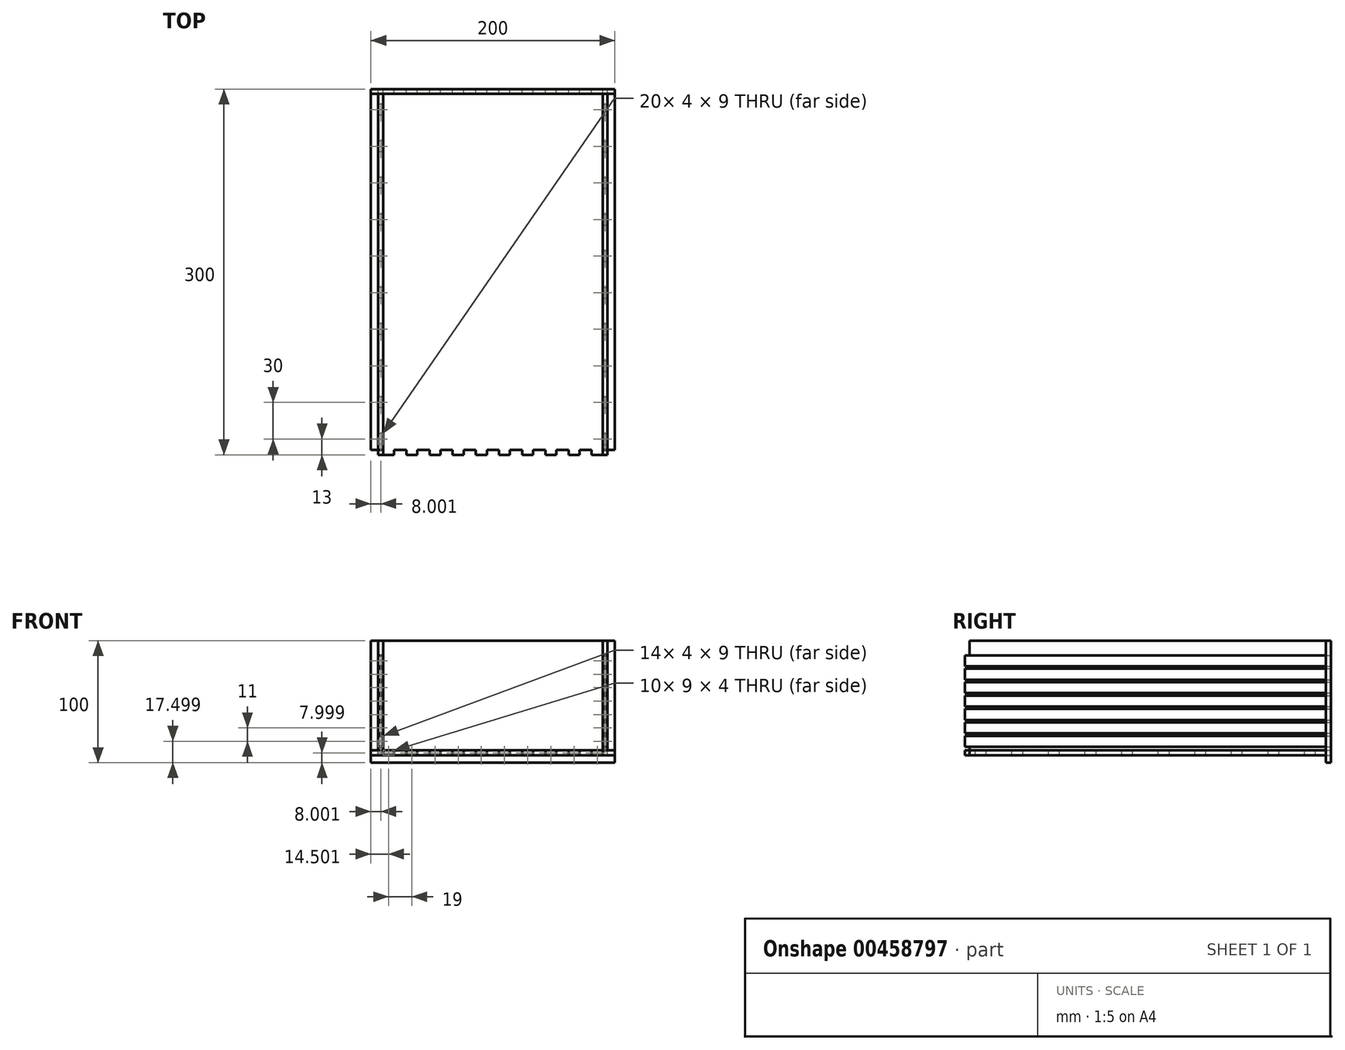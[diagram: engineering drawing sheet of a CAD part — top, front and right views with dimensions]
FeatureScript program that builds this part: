
annotation { "Feature Type Name" : "Feature", "Feature Type Description" : "" }
export const myFeature = defineFeature(function(context is Context, id is Id, definition is map)
    precondition{}
    {
        {
            var Q0;
            Q0=qCreatedBy(makeId("Front.planeOp"),FACE);
            var sketch = newSketch(context, id + "F0", { "sketchPlane" : qUnion([Q0])});
            skLineSegment(sketch, "E0.bottom", {"start": v(-98.88, 5.23) * mm, "end": v(101.12, 5.23) * mm});
            skLineSegment(sketch, "E0.top", {"start": v(-98.88, -94.77) * mm, "end": v(101.12, -94.77) * mm});
            skLineSegment(sketch, "E0.left", {"start": v(-98.88, 5.23) * mm, "end": v(-98.88, -94.77) * mm});
            skLineSegment(sketch, "E0.right", {"start": v(101.12, 5.23) * mm, "end": v(101.12, -94.77) * mm});
            skLineSegment(sketch, "E1.0", {"start": v(-88.88, -4.77) * mm, "end": v(91.12, -4.77) * mm, "construction": true});
            skLineSegment(sketch, "E1.2", {"start": v(-88.88, -84.77) * mm, "end": v(91.12, -84.77) * mm, "construction": true});
            skLineSegment(sketch, "E2.bottom", {"start": v(-88.88, -4.77) * mm, "end": v(-79.88, -4.77) * mm});
            skLineSegment(sketch, "E3.direction1", {"start": v(-88.88, -4.77) * mm, "end": v(-69.88, -4.77) * mm, "construction": true});
            skLineSegment(sketch, "E4.0.9.0", {"start": v(82.12, -4.77) * mm, "end": v(91.12, -4.77) * mm});
            skLineSegment(sketch, "E5", {"start": v(-98.88, -44.77) * mm, "end": v(101.12, -44.77) * mm, "construction": true});
            skLineSegment(sketch, "E6.MirrorCS", {"start": v(-88.88, -84.77) * mm, "end": v(-88.88, -88.77) * mm});
            skLineSegment(sketch, "E7.MirrorCS", {"start": v(-79.88, -84.77) * mm, "end": v(-79.88, -88.77) * mm});
            skLineSegment(sketch, "E8.MirrorCS", {"start": v(-88.88, -88.77) * mm, "end": v(-79.88, -88.77) * mm});
            skLineSegment(sketch, "E9.MirrorCS", {"start": v(-88.88, -84.77) * mm, "end": v(-79.88, -84.77) * mm});
            skLineSegment(sketch, "E10.1.0.0", {"start": v(-60.88, -84.77) * mm, "end": v(-60.88, -88.77) * mm});
            skLineSegment(sketch, "E10.1.0.1", {"start": v(-69.88, -88.77) * mm, "end": v(-60.88, -88.77) * mm});
            skLineSegment(sketch, "E10.1.0.2", {"start": v(-69.88, -84.77) * mm, "end": v(-69.88, -88.77) * mm});
            skLineSegment(sketch, "E10.1.0.3", {"start": v(-69.88, -84.77) * mm, "end": v(-60.88, -84.77) * mm});
            skLineSegment(sketch, "E10.2.0.0", {"start": v(-41.88, -84.77) * mm, "end": v(-41.88, -88.77) * mm});
            skLineSegment(sketch, "E10.2.0.1", {"start": v(-50.88, -88.77) * mm, "end": v(-41.88, -88.77) * mm});
            skLineSegment(sketch, "E10.2.0.2", {"start": v(-50.88, -84.77) * mm, "end": v(-50.88, -88.77) * mm});
            skLineSegment(sketch, "E10.2.0.3", {"start": v(-50.88, -84.77) * mm, "end": v(-41.88, -84.77) * mm});
            skLineSegment(sketch, "E10.3.0.0", {"start": v(-22.88, -84.77) * mm, "end": v(-22.88, -88.77) * mm});
            skLineSegment(sketch, "E10.3.0.1", {"start": v(-31.88, -88.77) * mm, "end": v(-22.88, -88.77) * mm});
            skLineSegment(sketch, "E10.3.0.2", {"start": v(-31.88, -84.77) * mm, "end": v(-31.88, -88.77) * mm});
            skLineSegment(sketch, "E10.3.0.3", {"start": v(-31.88, -84.77) * mm, "end": v(-22.88, -84.77) * mm});
            skLineSegment(sketch, "E10.4.0.0", {"start": v(-3.88, -84.77) * mm, "end": v(-3.88, -88.77) * mm});
            skLineSegment(sketch, "E10.4.0.1", {"start": v(-12.88, -88.77) * mm, "end": v(-3.88, -88.77) * mm});
            skLineSegment(sketch, "E10.4.0.2", {"start": v(-12.88, -84.77) * mm, "end": v(-12.88, -88.77) * mm});
            skLineSegment(sketch, "E10.4.0.3", {"start": v(-12.88, -84.77) * mm, "end": v(-3.88, -84.77) * mm});
            skLineSegment(sketch, "E10.5.0.0", {"start": v(15.12, -84.77) * mm, "end": v(15.12, -88.77) * mm});
            skLineSegment(sketch, "E10.5.0.1", {"start": v(6.12, -88.77) * mm, "end": v(15.12, -88.77) * mm});
            skLineSegment(sketch, "E10.5.0.2", {"start": v(6.12, -84.77) * mm, "end": v(6.12, -88.77) * mm});
            skLineSegment(sketch, "E10.5.0.3", {"start": v(6.12, -84.77) * mm, "end": v(15.12, -84.77) * mm});
            skLineSegment(sketch, "E10.6.0.0", {"start": v(34.12, -84.77) * mm, "end": v(34.12, -88.77) * mm});
            skLineSegment(sketch, "E10.6.0.1", {"start": v(25.12, -88.77) * mm, "end": v(34.12, -88.77) * mm});
            skLineSegment(sketch, "E10.6.0.2", {"start": v(25.12, -84.77) * mm, "end": v(25.12, -88.77) * mm});
            skLineSegment(sketch, "E10.6.0.3", {"start": v(25.12, -84.77) * mm, "end": v(34.12, -84.77) * mm});
            skLineSegment(sketch, "E10.7.0.0", {"start": v(53.12, -84.77) * mm, "end": v(53.12, -88.77) * mm});
            skLineSegment(sketch, "E10.7.0.1", {"start": v(44.12, -88.77) * mm, "end": v(53.12, -88.77) * mm});
            skLineSegment(sketch, "E10.7.0.2", {"start": v(44.12, -84.77) * mm, "end": v(44.12, -88.77) * mm});
            skLineSegment(sketch, "E10.7.0.3", {"start": v(44.12, -84.77) * mm, "end": v(53.12, -84.77) * mm});
            skLineSegment(sketch, "E10.8.0.0", {"start": v(72.12, -84.77) * mm, "end": v(72.12, -88.77) * mm});
            skLineSegment(sketch, "E10.8.0.1", {"start": v(63.12, -88.77) * mm, "end": v(72.12, -88.77) * mm});
            skLineSegment(sketch, "E10.8.0.2", {"start": v(63.12, -84.77) * mm, "end": v(63.12, -88.77) * mm});
            skLineSegment(sketch, "E10.8.0.3", {"start": v(63.12, -84.77) * mm, "end": v(72.12, -84.77) * mm});
            skLineSegment(sketch, "E10.9.0.0", {"start": v(91.12, -84.77) * mm, "end": v(91.12, -88.77) * mm});
            skLineSegment(sketch, "E10.9.0.1", {"start": v(82.12, -88.77) * mm, "end": v(91.12, -88.77) * mm});
            skLineSegment(sketch, "E10.9.0.2", {"start": v(82.12, -84.77) * mm, "end": v(82.12, -88.77) * mm});
            skLineSegment(sketch, "E10.9.0.3", {"start": v(82.12, -84.77) * mm, "end": v(91.12, -84.77) * mm});
            skLineSegment(sketch, "E10.direction1", {"start": v(-79.88, -88.77) * mm, "end": v(-60.88, -88.77) * mm, "construction": true});
            skLineSegment(sketch, "E11.bottom", {"start": v(-88.88, -81.77) * mm, "end": v(-92.88, -81.77) * mm});
            skLineSegment(sketch, "E11.top", {"start": v(-88.88, -72.77) * mm, "end": v(-92.88, -72.77) * mm});
            skLineSegment(sketch, "E11.left", {"start": v(-88.88, -81.77) * mm, "end": v(-88.88, -72.77) * mm});
            skLineSegment(sketch, "E11.right", {"start": v(-92.88, -81.77) * mm, "end": v(-92.88, -72.77) * mm});
            skLineSegment(sketch, "E12.0.1.0", {"start": v(-88.88, -61.77) * mm, "end": v(-92.88, -61.77) * mm});
            skLineSegment(sketch, "E12.0.1.1", {"start": v(-92.88, -70.77) * mm, "end": v(-92.88, -61.77) * mm});
            skLineSegment(sketch, "E12.0.1.2", {"start": v(-88.88, -70.77) * mm, "end": v(-92.88, -70.77) * mm});
            skLineSegment(sketch, "E12.0.1.3", {"start": v(-88.88, -70.77) * mm, "end": v(-88.88, -61.77) * mm});
            skLineSegment(sketch, "E12.0.2.0", {"start": v(-88.88, -50.77) * mm, "end": v(-92.88, -50.77) * mm});
            skLineSegment(sketch, "E12.0.2.1", {"start": v(-92.88, -59.77) * mm, "end": v(-92.88, -50.77) * mm});
            skLineSegment(sketch, "E12.0.2.2", {"start": v(-88.88, -59.77) * mm, "end": v(-92.88, -59.77) * mm});
            skLineSegment(sketch, "E12.0.2.3", {"start": v(-88.88, -59.77) * mm, "end": v(-88.88, -50.77) * mm});
            skLineSegment(sketch, "E12.0.3.0", {"start": v(-88.88, -39.77) * mm, "end": v(-92.88, -39.77) * mm});
            skLineSegment(sketch, "E12.0.3.1", {"start": v(-92.88, -48.77) * mm, "end": v(-92.88, -39.77) * mm});
            skLineSegment(sketch, "E12.0.3.2", {"start": v(-88.88, -48.77) * mm, "end": v(-92.88, -48.77) * mm});
            skLineSegment(sketch, "E12.0.3.3", {"start": v(-88.88, -48.77) * mm, "end": v(-88.88, -39.77) * mm});
            skLineSegment(sketch, "E12.0.4.0", {"start": v(-88.88, -28.77) * mm, "end": v(-92.88, -28.77) * mm});
            skLineSegment(sketch, "E12.0.4.1", {"start": v(-92.88, -37.77) * mm, "end": v(-92.88, -28.77) * mm});
            skLineSegment(sketch, "E12.0.4.2", {"start": v(-88.88, -37.77) * mm, "end": v(-92.88, -37.77) * mm});
            skLineSegment(sketch, "E12.0.4.3", {"start": v(-88.88, -37.77) * mm, "end": v(-88.88, -28.77) * mm});
            skLineSegment(sketch, "E12.0.5.0", {"start": v(-88.88, -17.77) * mm, "end": v(-92.88, -17.77) * mm});
            skLineSegment(sketch, "E12.0.5.1", {"start": v(-92.88, -26.77) * mm, "end": v(-92.88, -17.77) * mm});
            skLineSegment(sketch, "E12.0.5.2", {"start": v(-88.88, -26.77) * mm, "end": v(-92.88, -26.77) * mm});
            skLineSegment(sketch, "E12.0.5.3", {"start": v(-88.88, -26.77) * mm, "end": v(-88.88, -17.77) * mm});
            skLineSegment(sketch, "E12.0.6.0", {"start": v(-88.88, -6.77) * mm, "end": v(-92.88, -6.77) * mm});
            skLineSegment(sketch, "E12.0.6.1", {"start": v(-92.88, -15.77) * mm, "end": v(-92.88, -6.77) * mm});
            skLineSegment(sketch, "E12.0.6.2", {"start": v(-88.88, -15.77) * mm, "end": v(-92.88, -15.77) * mm});
            skLineSegment(sketch, "E12.0.6.3", {"start": v(-88.88, -15.77) * mm, "end": v(-88.88, -6.77) * mm});
            skLineSegment(sketch, "E12.direction1", {"start": v(-92.88, -72.77) * mm, "end": v(-67.88, -72.77) * mm, "construction": true});
            skLineSegment(sketch, "E12.direction2", {"start": v(-92.88, -72.77) * mm, "end": v(-92.88, -61.77) * mm, "construction": true});
            skLineSegment(sketch, "E13", {"start": v(1.12, 5.23) * mm, "end": v(1.12, -94.77) * mm, "construction": true});
            skLineSegment(sketch, "E14.MirrorCS", {"start": v(95.12, -81.77) * mm, "end": v(95.12, -72.77) * mm});
            skLineSegment(sketch, "E15.MirrorCS", {"start": v(91.12, -81.77) * mm, "end": v(95.12, -81.77) * mm});
            skLineSegment(sketch, "E16.MirrorCS", {"start": v(91.12, -81.77) * mm, "end": v(91.12, -72.77) * mm});
            skLineSegment(sketch, "E17.MirrorCS", {"start": v(95.12, -72.77) * mm, "end": v(70.12, -72.77) * mm, "construction": true});
            skLineSegment(sketch, "E18.MirrorCS", {"start": v(91.12, -72.77) * mm, "end": v(95.12, -72.77) * mm});
            skLineSegment(sketch, "E19.0.1.0", {"start": v(91.12, -70.77) * mm, "end": v(91.12, -61.77) * mm});
            skLineSegment(sketch, "E19.0.1.1", {"start": v(91.12, -61.77) * mm, "end": v(95.12, -61.77) * mm});
            skLineSegment(sketch, "E19.0.1.2", {"start": v(95.12, -70.77) * mm, "end": v(95.12, -61.77) * mm});
            skLineSegment(sketch, "E19.0.1.3", {"start": v(91.12, -70.77) * mm, "end": v(95.12, -70.77) * mm});
            skLineSegment(sketch, "E19.0.2.0", {"start": v(91.12, -59.77) * mm, "end": v(91.12, -50.77) * mm});
            skLineSegment(sketch, "E19.0.2.1", {"start": v(91.12, -50.77) * mm, "end": v(95.12, -50.77) * mm});
            skLineSegment(sketch, "E19.0.2.2", {"start": v(95.12, -59.77) * mm, "end": v(95.12, -50.77) * mm});
            skLineSegment(sketch, "E19.0.2.3", {"start": v(91.12, -59.77) * mm, "end": v(95.12, -59.77) * mm});
            skLineSegment(sketch, "E19.0.3.0", {"start": v(91.12, -48.77) * mm, "end": v(91.12, -39.77) * mm});
            skLineSegment(sketch, "E19.0.3.1", {"start": v(91.12, -39.77) * mm, "end": v(95.12, -39.77) * mm});
            skLineSegment(sketch, "E19.0.3.2", {"start": v(95.12, -48.77) * mm, "end": v(95.12, -39.77) * mm});
            skLineSegment(sketch, "E19.0.3.3", {"start": v(91.12, -48.77) * mm, "end": v(95.12, -48.77) * mm});
            skLineSegment(sketch, "E19.0.4.0", {"start": v(91.12, -37.77) * mm, "end": v(91.12, -28.77) * mm});
            skLineSegment(sketch, "E19.0.4.1", {"start": v(91.12, -28.77) * mm, "end": v(95.12, -28.77) * mm});
            skLineSegment(sketch, "E19.0.4.2", {"start": v(95.12, -37.77) * mm, "end": v(95.12, -28.77) * mm});
            skLineSegment(sketch, "E19.0.4.3", {"start": v(91.12, -37.77) * mm, "end": v(95.12, -37.77) * mm});
            skLineSegment(sketch, "E19.0.5.0", {"start": v(91.12, -26.77) * mm, "end": v(91.12, -17.77) * mm});
            skLineSegment(sketch, "E19.0.5.1", {"start": v(91.12, -17.77) * mm, "end": v(95.12, -17.77) * mm});
            skLineSegment(sketch, "E19.0.5.2", {"start": v(95.12, -26.77) * mm, "end": v(95.12, -17.77) * mm});
            skLineSegment(sketch, "E19.0.5.3", {"start": v(91.12, -26.77) * mm, "end": v(95.12, -26.77) * mm});
            skLineSegment(sketch, "E19.0.6.0", {"start": v(91.12, -15.77) * mm, "end": v(91.12, -6.77) * mm});
            skLineSegment(sketch, "E19.0.6.1", {"start": v(91.12, -6.77) * mm, "end": v(95.12, -6.77) * mm});
            skLineSegment(sketch, "E19.0.6.2", {"start": v(95.12, -15.77) * mm, "end": v(95.12, -6.77) * mm});
            skLineSegment(sketch, "E19.0.6.3", {"start": v(91.12, -15.77) * mm, "end": v(95.12, -15.77) * mm});
            skLineSegment(sketch, "E19.direction1", {"start": v(91.12, -81.77) * mm, "end": v(116.12, -81.77) * mm, "construction": true});
            skLineSegment(sketch, "E19.direction2", {"start": v(91.12, -81.77) * mm, "end": v(91.12, -70.77) * mm, "construction": true});
            skLineSegment(sketch, "E20", {"start": v(-84.38, -84.77) * mm, "end": v(-84.38, 5.23) * mm, "construction": true});
            skLineSegment(sketch, "E21.MirrorCS", {"start": v(86.62, -84.77) * mm, "end": v(86.62, 5.23) * mm, "construction": true});
            skSolve(sketch);
        }
        {
            var Q0;
            Q0=makeQuery(id+"F0.imprint","IMPRINT",FACE,{"disambiguationData":[TD([[makeQuery(id+"F0.imprint","IMPRINT",EDGE,{"derivedFrom":sQuery(id+"F0.wireOp",EDGE,"E0.bottom")}),-1.0]])]});
            extrude(context, id + "F1", {"entities" : qUnion([Q0]), "depth" : 4 * mm});
        }
        {
            var Q0;
            Q0=makeQuery(id+"F0.imprint","IMPRINT",FACE,{"disambiguationData":[TD([[makeQuery(id+"F0.imprint","IMPRINT",EDGE,{"derivedFrom":sQuery(id+"F0.wireOp",EDGE,"E10.8.0.0")}),-1.0]])]});
            var Q1;
            Q1=makeQuery(id+"F0.imprint","IMPRINT",FACE,{"disambiguationData":[TD([[makeQuery(id+"F0.imprint","IMPRINT",EDGE,{"derivedFrom":sQuery(id+"F0.wireOp",EDGE,"E10.7.0.0")}),-1.0]])]});
            var Q2;
            Q2=makeQuery(id+"F0.imprint","IMPRINT",FACE,{"disambiguationData":[TD([[makeQuery(id+"F0.imprint","IMPRINT",EDGE,{"derivedFrom":sQuery(id+"F0.wireOp",EDGE,"E10.9.0.0")}),-1.0]])]});
            var Q3;
            Q3=makeQuery(id+"F0.imprint","IMPRINT",FACE,{"disambiguationData":[TD([[makeQuery(id+"F0.imprint","IMPRINT",EDGE,{"derivedFrom":sQuery(id+"F0.wireOp",EDGE,"E10.6.0.0")}),-1.0]])]});
            var Q4;
            Q4=makeQuery(id+"F0.imprint","IMPRINT",FACE,{"disambiguationData":[TD([[makeQuery(id+"F0.imprint","IMPRINT",EDGE,{"derivedFrom":sQuery(id+"F0.wireOp",EDGE,"E10.5.0.0")}),-1.0]])]});
            var Q5;
            Q5=makeQuery(id+"F0.imprint","IMPRINT",FACE,{"disambiguationData":[TD([[makeQuery(id+"F0.imprint","IMPRINT",EDGE,{"derivedFrom":sQuery(id+"F0.wireOp",EDGE,"E10.4.0.0")}),-1.0]])]});
            var Q6;
            Q6=makeQuery(id+"F0.imprint","IMPRINT",FACE,{"disambiguationData":[TD([[makeQuery(id+"F0.imprint","IMPRINT",EDGE,{"derivedFrom":sQuery(id+"F0.wireOp",EDGE,"E10.3.0.0")}),-1.0]])]});
            var Q7;
            Q7=makeQuery(id+"F0.imprint","IMPRINT",FACE,{"disambiguationData":[TD([[makeQuery(id+"F0.imprint","IMPRINT",EDGE,{"derivedFrom":sQuery(id+"F0.wireOp",EDGE,"E10.2.0.0")}),-1.0]])]});
            var Q8;
            Q8=makeQuery(id+"F0.imprint","IMPRINT",FACE,{"disambiguationData":[TD([[makeQuery(id+"F0.imprint","IMPRINT",EDGE,{"derivedFrom":sQuery(id+"F0.wireOp",EDGE,"E10.1.0.0")}),-1.0]])]});
            var Q9;
            Q9=makeQuery(id+"F0.imprint","IMPRINT",FACE,{"disambiguationData":[TD([[makeQuery(id+"F0.imprint","IMPRINT",EDGE,{"derivedFrom":sQuery(id+"F0.wireOp",EDGE,"E6.MirrorCS")}),1.0]])]});
            extrude(context, id + "F2", {"entities" : qUnion([Q0, Q1, Q2, Q3, Q4, Q5, Q6, Q7, Q8, Q9]), "depth" : 300 * mm});
        }
        {
            var Q0;
            Q0=makeQuery(id+"F1.opExtrude","CAP_FACE",FACE,{"disambiguationData":[OSD([sQuery(id+"F0.wireOp",EDGE,"E0.bottom"),sQuery(id+"F0.wireOp",EDGE,"E0.top"),sQuery(id+"F0.wireOp",EDGE,"E0.left"),sQuery(id+"F0.wireOp",EDGE,"E0.right"),sQuery(id+"F0.wireOp",EDGE,"E6.MirrorCS"),sQuery(id+"F0.wireOp",EDGE,"E7.MirrorCS"),sQuery(id+"F0.wireOp",EDGE,"E8.MirrorCS"),sQuery(id+"F0.wireOp",EDGE,"E9.MirrorCS"),sQuery(id+"F0.wireOp",EDGE,"E10.1.0.0"),sQuery(id+"F0.wireOp",EDGE,"E10.1.0.1"),sQuery(id+"F0.wireOp",EDGE,"E10.1.0.2"),sQuery(id+"F0.wireOp",EDGE,"E10.1.0.3"),sQuery(id+"F0.wireOp",EDGE,"E10.2.0.0"),sQuery(id+"F0.wireOp",EDGE,"E10.2.0.1"),sQuery(id+"F0.wireOp",EDGE,"E10.2.0.2"),sQuery(id+"F0.wireOp",EDGE,"E10.2.0.3"),sQuery(id+"F0.wireOp",EDGE,"E10.3.0.0"),sQuery(id+"F0.wireOp",EDGE,"E10.3.0.1"),sQuery(id+"F0.wireOp",EDGE,"E10.3.0.2"),sQuery(id+"F0.wireOp",EDGE,"E10.3.0.3"),sQuery(id+"F0.wireOp",EDGE,"E10.4.0.0"),sQuery(id+"F0.wireOp",EDGE,"E10.4.0.1"),sQuery(id+"F0.wireOp",EDGE,"E10.4.0.2"),sQuery(id+"F0.wireOp",EDGE,"E10.4.0.3"),sQuery(id+"F0.wireOp",EDGE,"E10.5.0.0"),sQuery(id+"F0.wireOp",EDGE,"E10.5.0.1"),sQuery(id+"F0.wireOp",EDGE,"E10.5.0.2"),sQuery(id+"F0.wireOp",EDGE,"E10.5.0.3"),sQuery(id+"F0.wireOp",EDGE,"E10.6.0.0"),sQuery(id+"F0.wireOp",EDGE,"E10.6.0.1"),sQuery(id+"F0.wireOp",EDGE,"E10.6.0.2"),sQuery(id+"F0.wireOp",EDGE,"E10.6.0.3"),sQuery(id+"F0.wireOp",EDGE,"E10.7.0.0"),sQuery(id+"F0.wireOp",EDGE,"E10.7.0.1"),sQuery(id+"F0.wireOp",EDGE,"E10.7.0.2"),sQuery(id+"F0.wireOp",EDGE,"E10.7.0.3"),sQuery(id+"F0.wireOp",EDGE,"E10.8.0.0"),sQuery(id+"F0.wireOp",EDGE,"E10.8.0.1"),sQuery(id+"F0.wireOp",EDGE,"E10.8.0.2"),sQuery(id+"F0.wireOp",EDGE,"E10.8.0.3"),sQuery(id+"F0.wireOp",EDGE,"E10.9.0.0"),sQuery(id+"F0.wireOp",EDGE,"E10.9.0.1"),sQuery(id+"F0.wireOp",EDGE,"E10.9.0.2"),sQuery(id+"F0.wireOp",EDGE,"E10.9.0.3"),sQuery(id+"F0.wireOp",EDGE,"E11.bottom"),sQuery(id+"F0.wireOp",EDGE,"E11.top"),sQuery(id+"F0.wireOp",EDGE,"E11.left"),sQuery(id+"F0.wireOp",EDGE,"E11.right"),sQuery(id+"F0.wireOp",EDGE,"E12.0.1.0"),sQuery(id+"F0.wireOp",EDGE,"E12.0.1.1"),sQuery(id+"F0.wireOp",EDGE,"E12.0.1.2"),sQuery(id+"F0.wireOp",EDGE,"E12.0.1.3"),sQuery(id+"F0.wireOp",EDGE,"E12.0.2.0"),sQuery(id+"F0.wireOp",EDGE,"E12.0.2.1"),sQuery(id+"F0.wireOp",EDGE,"E12.0.2.2"),sQuery(id+"F0.wireOp",EDGE,"E12.0.2.3"),sQuery(id+"F0.wireOp",EDGE,"E12.0.3.0"),sQuery(id+"F0.wireOp",EDGE,"E12.0.3.1"),sQuery(id+"F0.wireOp",EDGE,"E12.0.3.2"),sQuery(id+"F0.wireOp",EDGE,"E12.0.3.3"),sQuery(id+"F0.wireOp",EDGE,"E12.0.4.0"),sQuery(id+"F0.wireOp",EDGE,"E12.0.4.1"),sQuery(id+"F0.wireOp",EDGE,"E12.0.4.2"),sQuery(id+"F0.wireOp",EDGE,"E12.0.4.3"),sQuery(id+"F0.wireOp",EDGE,"E12.0.5.0"),sQuery(id+"F0.wireOp",EDGE,"E12.0.5.1"),sQuery(id+"F0.wireOp",EDGE,"E12.0.5.2"),sQuery(id+"F0.wireOp",EDGE,"E12.0.5.3"),sQuery(id+"F0.wireOp",EDGE,"E12.0.6.0"),sQuery(id+"F0.wireOp",EDGE,"E12.0.6.1"),sQuery(id+"F0.wireOp",EDGE,"E12.0.6.2"),sQuery(id+"F0.wireOp",EDGE,"E12.0.6.3"),sQuery(id+"F0.wireOp",EDGE,"E14.MirrorCS"),sQuery(id+"F0.wireOp",EDGE,"E15.MirrorCS"),sQuery(id+"F0.wireOp",EDGE,"E16.MirrorCS"),sQuery(id+"F0.wireOp",EDGE,"E18.MirrorCS"),sQuery(id+"F0.wireOp",EDGE,"E19.0.1.0"),sQuery(id+"F0.wireOp",EDGE,"E19.0.1.1"),sQuery(id+"F0.wireOp",EDGE,"E19.0.1.2"),sQuery(id+"F0.wireOp",EDGE,"E19.0.1.3"),sQuery(id+"F0.wireOp",EDGE,"E19.0.2.0"),sQuery(id+"F0.wireOp",EDGE,"E19.0.2.1"),sQuery(id+"F0.wireOp",EDGE,"E19.0.2.2"),sQuery(id+"F0.wireOp",EDGE,"E19.0.2.3"),sQuery(id+"F0.wireOp",EDGE,"E19.0.3.0"),sQuery(id+"F0.wireOp",EDGE,"E19.0.3.1"),sQuery(id+"F0.wireOp",EDGE,"E19.0.3.2"),sQuery(id+"F0.wireOp",EDGE,"E19.0.3.3"),sQuery(id+"F0.wireOp",EDGE,"E19.0.4.0"),sQuery(id+"F0.wireOp",EDGE,"E19.0.4.1"),sQuery(id+"F0.wireOp",EDGE,"E19.0.4.2"),sQuery(id+"F0.wireOp",EDGE,"E19.0.4.3"),sQuery(id+"F0.wireOp",EDGE,"E19.0.5.0"),sQuery(id+"F0.wireOp",EDGE,"E19.0.5.1"),sQuery(id+"F0.wireOp",EDGE,"E19.0.5.2"),sQuery(id+"F0.wireOp",EDGE,"E19.0.5.3"),sQuery(id+"F0.wireOp",EDGE,"E19.0.6.0"),sQuery(id+"F0.wireOp",EDGE,"E19.0.6.1"),sQuery(id+"F0.wireOp",EDGE,"E19.0.6.2"),sQuery(id+"F0.wireOp",EDGE,"E19.0.6.3")])],"isStart":false});
            var sketch = newSketch(context, id + "F3", { "sketchPlane" : qUnion([Q0])});
            skLineSegment(sketch, "E22.bottom", {"start": v(-79.88, -84.77) * mm, "end": v(-69.88, -84.77) * mm});
            skLineSegment(sketch, "E22.top", {"start": v(-79.88, -88.77) * mm, "end": v(-69.88, -88.77) * mm});
            skLineSegment(sketch, "E22.left", {"start": v(-79.88, -84.77) * mm, "end": v(-79.88, -88.77) * mm});
            skLineSegment(sketch, "E22.right", {"start": v(-69.88, -84.77) * mm, "end": v(-69.88, -88.77) * mm});
            skLineSegment(sketch, "E23.1.0.0", {"start": v(-60.88, -84.77) * mm, "end": v(-50.88, -84.77) * mm});
            skLineSegment(sketch, "E23.1.0.1", {"start": v(-60.88, -84.77) * mm, "end": v(-60.88, -88.77) * mm});
            skLineSegment(sketch, "E23.1.0.2", {"start": v(-60.88, -88.77) * mm, "end": v(-50.88, -88.77) * mm});
            skLineSegment(sketch, "E23.1.0.3", {"start": v(-50.88, -84.77) * mm, "end": v(-50.88, -88.77) * mm});
            skLineSegment(sketch, "E23.2.0.0", {"start": v(-41.88, -84.77) * mm, "end": v(-31.88, -84.77) * mm});
            skLineSegment(sketch, "E23.2.0.1", {"start": v(-41.88, -84.77) * mm, "end": v(-41.88, -88.77) * mm});
            skLineSegment(sketch, "E23.2.0.2", {"start": v(-41.88, -88.77) * mm, "end": v(-31.88, -88.77) * mm});
            skLineSegment(sketch, "E23.2.0.3", {"start": v(-31.88, -84.77) * mm, "end": v(-31.88, -88.77) * mm});
            skLineSegment(sketch, "E23.3.0.0", {"start": v(-22.88, -84.77) * mm, "end": v(-12.88, -84.77) * mm});
            skLineSegment(sketch, "E23.3.0.1", {"start": v(-22.88, -84.77) * mm, "end": v(-22.88, -88.77) * mm});
            skLineSegment(sketch, "E23.3.0.2", {"start": v(-22.88, -88.77) * mm, "end": v(-12.88, -88.77) * mm});
            skLineSegment(sketch, "E23.3.0.3", {"start": v(-12.88, -84.77) * mm, "end": v(-12.88, -88.77) * mm});
            skLineSegment(sketch, "E23.4.0.0", {"start": v(-3.88, -84.77) * mm, "end": v(6.12, -84.77) * mm});
            skLineSegment(sketch, "E23.4.0.1", {"start": v(-3.88, -84.77) * mm, "end": v(-3.88, -88.77) * mm});
            skLineSegment(sketch, "E23.4.0.2", {"start": v(-3.88, -88.77) * mm, "end": v(6.12, -88.77) * mm});
            skLineSegment(sketch, "E23.4.0.3", {"start": v(6.12, -84.77) * mm, "end": v(6.12, -88.77) * mm});
            skLineSegment(sketch, "E23.5.0.0", {"start": v(15.12, -84.77) * mm, "end": v(25.12, -84.77) * mm});
            skLineSegment(sketch, "E23.5.0.1", {"start": v(15.12, -84.77) * mm, "end": v(15.12, -88.77) * mm});
            skLineSegment(sketch, "E23.5.0.2", {"start": v(15.12, -88.77) * mm, "end": v(25.12, -88.77) * mm});
            skLineSegment(sketch, "E23.5.0.3", {"start": v(25.12, -84.77) * mm, "end": v(25.12, -88.77) * mm});
            skLineSegment(sketch, "E23.6.0.0", {"start": v(34.12, -84.77) * mm, "end": v(44.12, -84.77) * mm});
            skLineSegment(sketch, "E23.6.0.1", {"start": v(34.12, -84.77) * mm, "end": v(34.12, -88.77) * mm});
            skLineSegment(sketch, "E23.6.0.2", {"start": v(34.12, -88.77) * mm, "end": v(44.12, -88.77) * mm});
            skLineSegment(sketch, "E23.6.0.3", {"start": v(44.12, -84.77) * mm, "end": v(44.12, -88.77) * mm});
            skLineSegment(sketch, "E23.7.0.0", {"start": v(53.12, -84.77) * mm, "end": v(63.12, -84.77) * mm});
            skLineSegment(sketch, "E23.7.0.1", {"start": v(53.12, -84.77) * mm, "end": v(53.12, -88.77) * mm});
            skLineSegment(sketch, "E23.7.0.2", {"start": v(53.12, -88.77) * mm, "end": v(63.12, -88.77) * mm});
            skLineSegment(sketch, "E23.7.0.3", {"start": v(63.12, -84.77) * mm, "end": v(63.12, -88.77) * mm});
            skLineSegment(sketch, "E23.8.0.0", {"start": v(72.12, -84.77) * mm, "end": v(82.12, -84.77) * mm});
            skLineSegment(sketch, "E23.8.0.1", {"start": v(72.12, -84.77) * mm, "end": v(72.12, -88.77) * mm});
            skLineSegment(sketch, "E23.8.0.2", {"start": v(72.12, -88.77) * mm, "end": v(82.12, -88.77) * mm});
            skLineSegment(sketch, "E23.8.0.3", {"start": v(82.12, -84.77) * mm, "end": v(82.12, -88.77) * mm});
            skLineSegment(sketch, "E23.direction1", {"start": v(-79.88, -84.77) * mm, "end": v(-60.88, -84.77) * mm, "construction": true});
            skSolve(sketch);
        }
        {
            var Q0;
            Q0=makeQuery(id+"F3.imprint","IMPRINT",FACE,{"disambiguationData":[TD([[makeQuery(id+"F3.imprint","IMPRINT",EDGE,{"derivedFrom":sQuery(id+"F3.wireOp",EDGE,"E22.bottom")}),-1.0]])]});
            var Q1;
            Q1=makeQuery(id+"F3.imprint","IMPRINT",FACE,{"disambiguationData":[TD([[makeQuery(id+"F3.imprint","IMPRINT",EDGE,{"derivedFrom":sQuery(id+"F3.wireOp",EDGE,"E23.1.0.0")}),-1.0]])]});
            var Q2;
            Q2=makeQuery(id+"F3.imprint","IMPRINT",FACE,{"disambiguationData":[TD([[makeQuery(id+"F3.imprint","IMPRINT",EDGE,{"derivedFrom":sQuery(id+"F3.wireOp",EDGE,"E23.2.0.0")}),-1.0]])]});
            var Q3;
            Q3=makeQuery(id+"F3.imprint","IMPRINT",FACE,{"disambiguationData":[TD([[makeQuery(id+"F3.imprint","IMPRINT",EDGE,{"derivedFrom":sQuery(id+"F3.wireOp",EDGE,"E23.3.0.0")}),-1.0]])]});
            var Q4;
            Q4=makeQuery(id+"F3.imprint","IMPRINT",FACE,{"disambiguationData":[TD([[makeQuery(id+"F3.imprint","IMPRINT",EDGE,{"derivedFrom":sQuery(id+"F3.wireOp",EDGE,"E23.4.0.0")}),-1.0]])]});
            var Q5;
            Q5=makeQuery(id+"F3.imprint","IMPRINT",FACE,{"disambiguationData":[TD([[makeQuery(id+"F3.imprint","IMPRINT",EDGE,{"derivedFrom":sQuery(id+"F3.wireOp",EDGE,"E23.6.0.0")}),-1.0]])]});
            var Q6;
            Q6=makeQuery(id+"F3.imprint","IMPRINT",FACE,{"disambiguationData":[TD([[makeQuery(id+"F3.imprint","IMPRINT",EDGE,{"derivedFrom":sQuery(id+"F3.wireOp",EDGE,"E23.7.0.0")}),-1.0]])]});
            var Q7;
            Q7=makeQuery(id+"F3.imprint","IMPRINT",FACE,{"disambiguationData":[TD([[makeQuery(id+"F3.imprint","IMPRINT",EDGE,{"derivedFrom":sQuery(id+"F3.wireOp",EDGE,"E23.8.0.0")}),-1.0]])]});
            var Q8;
            Q8=makeQuery(id+"F3.imprint","IMPRINT",FACE,{"disambiguationData":[TD([[makeQuery(id+"F3.imprint","IMPRINT",EDGE,{"derivedFrom":sQuery(id+"F3.wireOp",EDGE,"E23.5.0.0")}),-1.0]])]});
            extrude(context, id + "F4", {"entities" : qUnion([Q0, Q1, Q2, Q3, Q4, Q5, Q6, Q7, Q8]), "depth" : 292 * mm});
        }
        {
            var Q0;
            Q0=makeQuery(id+"F2.opExtrude","SWEPT_BODY",BODY,{"disambiguationData":[OSD([sQuery(id+"F0.wireOp",EDGE,"E6.MirrorCS"),sQuery(id+"F0.wireOp",EDGE,"E7.MirrorCS"),sQuery(id+"F0.wireOp",EDGE,"E8.MirrorCS"),sQuery(id+"F0.wireOp",EDGE,"E9.MirrorCS")])]});
            var Q1;
            Q1=makeQuery(id+"F2.opExtrude","SWEPT_BODY",BODY,{"disambiguationData":[OSD([sQuery(id+"F0.wireOp",EDGE,"E10.1.0.0"),sQuery(id+"F0.wireOp",EDGE,"E10.1.0.1"),sQuery(id+"F0.wireOp",EDGE,"E10.1.0.2"),sQuery(id+"F0.wireOp",EDGE,"E10.1.0.3")])]});
            var Q2;
            Q2=makeQuery(id+"F2.opExtrude","SWEPT_BODY",BODY,{"disambiguationData":[OSD([sQuery(id+"F0.wireOp",EDGE,"E10.2.0.0"),sQuery(id+"F0.wireOp",EDGE,"E10.2.0.1"),sQuery(id+"F0.wireOp",EDGE,"E10.2.0.2"),sQuery(id+"F0.wireOp",EDGE,"E10.2.0.3")])]});
            var Q3;
            Q3=makeQuery(id+"F2.opExtrude","SWEPT_BODY",BODY,{"disambiguationData":[OSD([sQuery(id+"F0.wireOp",EDGE,"E10.3.0.0"),sQuery(id+"F0.wireOp",EDGE,"E10.3.0.1"),sQuery(id+"F0.wireOp",EDGE,"E10.3.0.2"),sQuery(id+"F0.wireOp",EDGE,"E10.3.0.3")])]});
            var Q4;
            Q4=makeQuery(id+"F2.opExtrude","SWEPT_BODY",BODY,{"disambiguationData":[OSD([sQuery(id+"F0.wireOp",EDGE,"E10.4.0.0"),sQuery(id+"F0.wireOp",EDGE,"E10.4.0.1"),sQuery(id+"F0.wireOp",EDGE,"E10.4.0.2"),sQuery(id+"F0.wireOp",EDGE,"E10.4.0.3")])]});
            var Q5;
            Q5=makeQuery(id+"F2.opExtrude","SWEPT_BODY",BODY,{"disambiguationData":[OSD([sQuery(id+"F0.wireOp",EDGE,"E10.5.0.0"),sQuery(id+"F0.wireOp",EDGE,"E10.5.0.1"),sQuery(id+"F0.wireOp",EDGE,"E10.5.0.2"),sQuery(id+"F0.wireOp",EDGE,"E10.5.0.3")])]});
            var Q6;
            Q6=makeQuery(id+"F2.opExtrude","SWEPT_BODY",BODY,{"disambiguationData":[OSD([sQuery(id+"F0.wireOp",EDGE,"E10.6.0.0"),sQuery(id+"F0.wireOp",EDGE,"E10.6.0.1"),sQuery(id+"F0.wireOp",EDGE,"E10.6.0.2"),sQuery(id+"F0.wireOp",EDGE,"E10.6.0.3")])]});
            var Q7;
            Q7=makeQuery(id+"F2.opExtrude","SWEPT_BODY",BODY,{"disambiguationData":[OSD([sQuery(id+"F0.wireOp",EDGE,"E10.7.0.0"),sQuery(id+"F0.wireOp",EDGE,"E10.7.0.1"),sQuery(id+"F0.wireOp",EDGE,"E10.7.0.2"),sQuery(id+"F0.wireOp",EDGE,"E10.7.0.3")])]});
            var Q8;
            Q8=makeQuery(id+"F2.opExtrude","SWEPT_BODY",BODY,{"disambiguationData":[OSD([sQuery(id+"F0.wireOp",EDGE,"E10.8.0.0"),sQuery(id+"F0.wireOp",EDGE,"E10.8.0.1"),sQuery(id+"F0.wireOp",EDGE,"E10.8.0.2"),sQuery(id+"F0.wireOp",EDGE,"E10.8.0.3")])]});
            var Q9;
            Q9=makeQuery(id+"F2.opExtrude","SWEPT_BODY",BODY,{"disambiguationData":[OSD([sQuery(id+"F0.wireOp",EDGE,"E10.9.0.0"),sQuery(id+"F0.wireOp",EDGE,"E10.9.0.1"),sQuery(id+"F0.wireOp",EDGE,"E10.9.0.2"),sQuery(id+"F0.wireOp",EDGE,"E10.9.0.3")])]});
            var Q10;
            Q10=makeQuery(id+"F4.opExtrude","SWEPT_BODY",BODY,{"disambiguationData":[OSD([sQuery(id+"F3.wireOp",EDGE,"E22.bottom"),sQuery(id+"F3.wireOp",EDGE,"E22.top"),sQuery(id+"F3.wireOp",EDGE,"E22.left"),sQuery(id+"F3.wireOp",EDGE,"E22.right")])]});
            var Q11;
            Q11=makeQuery(id+"F4.opExtrude","SWEPT_BODY",BODY,{"disambiguationData":[OSD([sQuery(id+"F3.wireOp",EDGE,"E23.1.0.0"),sQuery(id+"F3.wireOp",EDGE,"E23.1.0.1"),sQuery(id+"F3.wireOp",EDGE,"E23.1.0.2"),sQuery(id+"F3.wireOp",EDGE,"E23.1.0.3")])]});
            var Q12;
            Q12=makeQuery(id+"F4.opExtrude","SWEPT_BODY",BODY,{"disambiguationData":[OSD([sQuery(id+"F3.wireOp",EDGE,"E23.4.0.0"),sQuery(id+"F3.wireOp",EDGE,"E23.4.0.1"),sQuery(id+"F3.wireOp",EDGE,"E23.4.0.2"),sQuery(id+"F3.wireOp",EDGE,"E23.4.0.3")])]});
            var Q13;
            Q13=makeQuery(id+"F4.opExtrude","SWEPT_BODY",BODY,{"disambiguationData":[OSD([sQuery(id+"F3.wireOp",EDGE,"E23.5.0.0"),sQuery(id+"F3.wireOp",EDGE,"E23.5.0.1"),sQuery(id+"F3.wireOp",EDGE,"E23.5.0.2"),sQuery(id+"F3.wireOp",EDGE,"E23.5.0.3")])]});
            var Q14;
            Q14=makeQuery(id+"F4.opExtrude","SWEPT_BODY",BODY,{"disambiguationData":[OSD([sQuery(id+"F3.wireOp",EDGE,"E23.3.0.0"),sQuery(id+"F3.wireOp",EDGE,"E23.3.0.1"),sQuery(id+"F3.wireOp",EDGE,"E23.3.0.2"),sQuery(id+"F3.wireOp",EDGE,"E23.3.0.3")])]});
            var Q15;
            Q15=makeQuery(id+"F4.opExtrude","SWEPT_BODY",BODY,{"disambiguationData":[OSD([sQuery(id+"F3.wireOp",EDGE,"E23.2.0.0"),sQuery(id+"F3.wireOp",EDGE,"E23.2.0.1"),sQuery(id+"F3.wireOp",EDGE,"E23.2.0.2"),sQuery(id+"F3.wireOp",EDGE,"E23.2.0.3")])]});
            var Q16;
            Q16=makeQuery(id+"F4.opExtrude","SWEPT_BODY",BODY,{"disambiguationData":[OSD([sQuery(id+"F3.wireOp",EDGE,"E23.7.0.0"),sQuery(id+"F3.wireOp",EDGE,"E23.7.0.1"),sQuery(id+"F3.wireOp",EDGE,"E23.7.0.2"),sQuery(id+"F3.wireOp",EDGE,"E23.7.0.3")])]});
            var Q17;
            Q17=makeQuery(id+"F4.opExtrude","SWEPT_BODY",BODY,{"disambiguationData":[OSD([sQuery(id+"F3.wireOp",EDGE,"E23.6.0.0"),sQuery(id+"F3.wireOp",EDGE,"E23.6.0.1"),sQuery(id+"F3.wireOp",EDGE,"E23.6.0.2"),sQuery(id+"F3.wireOp",EDGE,"E23.6.0.3")])]});
            var Q18;
            Q18=makeQuery(id+"F4.opExtrude","SWEPT_BODY",BODY,{"disambiguationData":[OSD([sQuery(id+"F3.wireOp",EDGE,"E23.8.0.0"),sQuery(id+"F3.wireOp",EDGE,"E23.8.0.1"),sQuery(id+"F3.wireOp",EDGE,"E23.8.0.2"),sQuery(id+"F3.wireOp",EDGE,"E23.8.0.3")])]});
            booleanBodies(context, id + "F5", {"operationType" : BooleanOperationType.UNION, "tools" : qUnion([Q0, Q1, Q2, Q3, Q4, Q5, Q6, Q7, Q8, Q9, Q10, Q11, Q12, Q13, Q14, Q15, Q16, Q17, Q18])});
        }
        {
            var Q0;
            Q0=makeQuery(id+"F2.opExtrude","SWEPT_FACE",FACE,{"disambiguationData":[OSD([sQuery(id+"F0.wireOp",EDGE,"E6.MirrorCS")])]});
            var sketch = newSketch(context, id + "F6", { "sketchPlane" : qUnion([Q0])});
            skLineSegment(sketch, "E24", {"start": v(4, -84.77) * mm, "end": v(4, -88.77) * mm});
            skLineSegment(sketch, "E25", {"start": v(296, -84.77) * mm, "end": v(296, -88.77) * mm});
            skSolve(sketch);
        }
        {
            var Q0;
            {var subQ0=sQuery(id+"F6.wireOp",EDGE,"E24");Q0=makeQuery(id+"F6.imprint","IMPRINT",FACE,{"disambiguationData":[TD([[makeQuery(id+"F6.imprint","IMPRINT",EDGE,{"derivedFrom":subQ0}),1.0]])]});}
            extrude(context, id + "F7", {"entities" : qUnion([Q0]), "depth" : 10 * mm});
        }
        {
            var Q0;
            Q0=makeQuery(id+"F2.opExtrude","SWEPT_BODY",BODY,{"disambiguationData":[OSD([sQuery(id+"F0.wireOp",EDGE,"E6.MirrorCS"),sQuery(id+"F0.wireOp",EDGE,"E7.MirrorCS"),sQuery(id+"F0.wireOp",EDGE,"E8.MirrorCS"),sQuery(id+"F0.wireOp",EDGE,"E9.MirrorCS")])]});
            var Q1;
            Q1=makeQuery(id+"F7.opExtrude","SWEPT_BODY",BODY,{"disambiguationData":[OSD([sQuery(id+"F0.wireOp",EDGE,"E6.MirrorCS"),sQuery(id+"F0.wireOp",EDGE,"E8.MirrorCS"),sQuery(id+"F0.wireOp",EDGE,"E9.MirrorCS")])]});
            booleanBodies(context, id + "F8", {"operationType" : BooleanOperationType.UNION, "tools" : qUnion([Q0, Q1])});
        }
        {
            var Q0;
            Q0=makeQuery(id+"F2.opExtrude","SWEPT_FACE",FACE,{"disambiguationData":[OSD([sQuery(id+"F0.wireOp",EDGE,"E10.9.0.0")])]});
            var sketch = newSketch(context, id + "F9", { "sketchPlane" : qUnion([Q0])});
            skLineSegment(sketch, "E26", {"start": v(13.3, -84.77) * mm, "end": v(13.3, -87.46) * mm});
            skLineSegment(sketch, "E27", {"start": v(-4, -84.77) * mm, "end": v(-4, -88.77) * mm});
            skLineSegment(sketch, "E28", {"start": v(-296, -84.77) * mm, "end": v(-296, -88.77) * mm});
            skSolve(sketch);
        }
        {
            var Q0;
            {var subQ0=sQuery(id+"F9.wireOp",EDGE,"E27");Q0=makeQuery(id+"F9.imprint","IMPRINT",FACE,{"disambiguationData":[TD([[makeQuery(id+"F9.imprint","IMPRINT",EDGE,{"derivedFrom":subQ0}),-1.0]])]});}
            extrude(context, id + "F10", {"entities" : qUnion([Q0]), "depth" : 10 * mm});
        }
        {
            var Q0;
            Q0=makeQuery(id+"F10.opExtrude","SWEPT_BODY",BODY,{"disambiguationData":[OSD([sQuery(id+"F0.wireOp",EDGE,"E10.9.0.0"),sQuery(id+"F0.wireOp",EDGE,"E10.9.0.1"),sQuery(id+"F0.wireOp",EDGE,"E10.9.0.3")])]});
            var Q1;
            Q1=makeQuery(id+"F2.opExtrude","SWEPT_BODY",BODY,{"disambiguationData":[OSD([sQuery(id+"F0.wireOp",EDGE,"E6.MirrorCS"),sQuery(id+"F0.wireOp",EDGE,"E7.MirrorCS"),sQuery(id+"F0.wireOp",EDGE,"E8.MirrorCS"),sQuery(id+"F0.wireOp",EDGE,"E9.MirrorCS")])]});
            booleanBodies(context, id + "F11", {"operationType" : BooleanOperationType.UNION, "tools" : qUnion([Q0, Q1])});
        }
        {
            var Q0;
            Q0=makeQuery(id+"F1.opExtrude","CAP_FACE",FACE,{"disambiguationData":[OSD([sQuery(id+"F0.wireOp",EDGE,"E0.bottom"),sQuery(id+"F0.wireOp",EDGE,"E0.top"),sQuery(id+"F0.wireOp",EDGE,"E0.left"),sQuery(id+"F0.wireOp",EDGE,"E0.right"),sQuery(id+"F0.wireOp",EDGE,"E6.MirrorCS"),sQuery(id+"F0.wireOp",EDGE,"E7.MirrorCS"),sQuery(id+"F0.wireOp",EDGE,"E8.MirrorCS"),sQuery(id+"F0.wireOp",EDGE,"E9.MirrorCS"),sQuery(id+"F0.wireOp",EDGE,"E10.1.0.0"),sQuery(id+"F0.wireOp",EDGE,"E10.1.0.1"),sQuery(id+"F0.wireOp",EDGE,"E10.1.0.2"),sQuery(id+"F0.wireOp",EDGE,"E10.1.0.3"),sQuery(id+"F0.wireOp",EDGE,"E10.2.0.0"),sQuery(id+"F0.wireOp",EDGE,"E10.2.0.1"),sQuery(id+"F0.wireOp",EDGE,"E10.2.0.2"),sQuery(id+"F0.wireOp",EDGE,"E10.2.0.3"),sQuery(id+"F0.wireOp",EDGE,"E10.3.0.0"),sQuery(id+"F0.wireOp",EDGE,"E10.3.0.1"),sQuery(id+"F0.wireOp",EDGE,"E10.3.0.2"),sQuery(id+"F0.wireOp",EDGE,"E10.3.0.3"),sQuery(id+"F0.wireOp",EDGE,"E10.4.0.0"),sQuery(id+"F0.wireOp",EDGE,"E10.4.0.1"),sQuery(id+"F0.wireOp",EDGE,"E10.4.0.2"),sQuery(id+"F0.wireOp",EDGE,"E10.4.0.3"),sQuery(id+"F0.wireOp",EDGE,"E10.5.0.0"),sQuery(id+"F0.wireOp",EDGE,"E10.5.0.1"),sQuery(id+"F0.wireOp",EDGE,"E10.5.0.2"),sQuery(id+"F0.wireOp",EDGE,"E10.5.0.3"),sQuery(id+"F0.wireOp",EDGE,"E10.6.0.0"),sQuery(id+"F0.wireOp",EDGE,"E10.6.0.1"),sQuery(id+"F0.wireOp",EDGE,"E10.6.0.2"),sQuery(id+"F0.wireOp",EDGE,"E10.6.0.3"),sQuery(id+"F0.wireOp",EDGE,"E10.7.0.0"),sQuery(id+"F0.wireOp",EDGE,"E10.7.0.1"),sQuery(id+"F0.wireOp",EDGE,"E10.7.0.2"),sQuery(id+"F0.wireOp",EDGE,"E10.7.0.3"),sQuery(id+"F0.wireOp",EDGE,"E10.8.0.0"),sQuery(id+"F0.wireOp",EDGE,"E10.8.0.1"),sQuery(id+"F0.wireOp",EDGE,"E10.8.0.2"),sQuery(id+"F0.wireOp",EDGE,"E10.8.0.3"),sQuery(id+"F0.wireOp",EDGE,"E10.9.0.0"),sQuery(id+"F0.wireOp",EDGE,"E10.9.0.1"),sQuery(id+"F0.wireOp",EDGE,"E10.9.0.2"),sQuery(id+"F0.wireOp",EDGE,"E10.9.0.3"),sQuery(id+"F0.wireOp",EDGE,"E11.bottom"),sQuery(id+"F0.wireOp",EDGE,"E11.top"),sQuery(id+"F0.wireOp",EDGE,"E11.left"),sQuery(id+"F0.wireOp",EDGE,"E11.right"),sQuery(id+"F0.wireOp",EDGE,"E12.0.1.0"),sQuery(id+"F0.wireOp",EDGE,"E12.0.1.1"),sQuery(id+"F0.wireOp",EDGE,"E12.0.1.2"),sQuery(id+"F0.wireOp",EDGE,"E12.0.1.3"),sQuery(id+"F0.wireOp",EDGE,"E12.0.2.0"),sQuery(id+"F0.wireOp",EDGE,"E12.0.2.1"),sQuery(id+"F0.wireOp",EDGE,"E12.0.2.2"),sQuery(id+"F0.wireOp",EDGE,"E12.0.2.3"),sQuery(id+"F0.wireOp",EDGE,"E12.0.3.0"),sQuery(id+"F0.wireOp",EDGE,"E12.0.3.1"),sQuery(id+"F0.wireOp",EDGE,"E12.0.3.2"),sQuery(id+"F0.wireOp",EDGE,"E12.0.3.3"),sQuery(id+"F0.wireOp",EDGE,"E12.0.4.0"),sQuery(id+"F0.wireOp",EDGE,"E12.0.4.1"),sQuery(id+"F0.wireOp",EDGE,"E12.0.4.2"),sQuery(id+"F0.wireOp",EDGE,"E12.0.4.3"),sQuery(id+"F0.wireOp",EDGE,"E12.0.5.0"),sQuery(id+"F0.wireOp",EDGE,"E12.0.5.1"),sQuery(id+"F0.wireOp",EDGE,"E12.0.5.2"),sQuery(id+"F0.wireOp",EDGE,"E12.0.5.3"),sQuery(id+"F0.wireOp",EDGE,"E12.0.6.0"),sQuery(id+"F0.wireOp",EDGE,"E12.0.6.1"),sQuery(id+"F0.wireOp",EDGE,"E12.0.6.2"),sQuery(id+"F0.wireOp",EDGE,"E12.0.6.3"),sQuery(id+"F0.wireOp",EDGE,"E14.MirrorCS"),sQuery(id+"F0.wireOp",EDGE,"E15.MirrorCS"),sQuery(id+"F0.wireOp",EDGE,"E16.MirrorCS"),sQuery(id+"F0.wireOp",EDGE,"E18.MirrorCS"),sQuery(id+"F0.wireOp",EDGE,"E19.0.1.0"),sQuery(id+"F0.wireOp",EDGE,"E19.0.1.1"),sQuery(id+"F0.wireOp",EDGE,"E19.0.1.2"),sQuery(id+"F0.wireOp",EDGE,"E19.0.1.3"),sQuery(id+"F0.wireOp",EDGE,"E19.0.2.0"),sQuery(id+"F0.wireOp",EDGE,"E19.0.2.1"),sQuery(id+"F0.wireOp",EDGE,"E19.0.2.2"),sQuery(id+"F0.wireOp",EDGE,"E19.0.2.3"),sQuery(id+"F0.wireOp",EDGE,"E19.0.3.0"),sQuery(id+"F0.wireOp",EDGE,"E19.0.3.1"),sQuery(id+"F0.wireOp",EDGE,"E19.0.3.2"),sQuery(id+"F0.wireOp",EDGE,"E19.0.3.3"),sQuery(id+"F0.wireOp",EDGE,"E19.0.4.0"),sQuery(id+"F0.wireOp",EDGE,"E19.0.4.1"),sQuery(id+"F0.wireOp",EDGE,"E19.0.4.2"),sQuery(id+"F0.wireOp",EDGE,"E19.0.4.3"),sQuery(id+"F0.wireOp",EDGE,"E19.0.5.0"),sQuery(id+"F0.wireOp",EDGE,"E19.0.5.1"),sQuery(id+"F0.wireOp",EDGE,"E19.0.5.2"),sQuery(id+"F0.wireOp",EDGE,"E19.0.5.3"),sQuery(id+"F0.wireOp",EDGE,"E19.0.6.0"),sQuery(id+"F0.wireOp",EDGE,"E19.0.6.1"),sQuery(id+"F0.wireOp",EDGE,"E19.0.6.2"),sQuery(id+"F0.wireOp",EDGE,"E19.0.6.3")])],"isStart":false});
            var sketch = newSketch(context, id + "F12", { "sketchPlane" : qUnion([Q0])});
            skLineSegment(sketch, "E29.bottom", {"start": v(-92.88, 5.23) * mm, "end": v(-88.88, 5.23) * mm});
            skLineSegment(sketch, "E29.top", {"start": v(-92.88, -84.77) * mm, "end": v(-88.88, -84.77) * mm});
            skLineSegment(sketch, "E29.left", {"start": v(-92.88, 5.23) * mm, "end": v(-92.88, -84.77) * mm});
            skLineSegment(sketch, "E29.right", {"start": v(-88.88, 5.23) * mm, "end": v(-88.88, -84.77) * mm});
            skLineSegment(sketch, "E30.MirrorCS", {"start": v(91.12, 5.23) * mm, "end": v(91.12, -84.77) * mm});
            skLineSegment(sketch, "E31.MirrorCS", {"start": v(95.12, 5.23) * mm, "end": v(95.12, -84.77) * mm});
            skLineSegment(sketch, "E32.bottom", {"start": v(-92.88, -6.77) * mm, "end": v(-88.88, -6.77) * mm});
            skLineSegment(sketch, "E32.top", {"start": v(-92.88, -15.77) * mm, "end": v(-88.88, -15.77) * mm});
            skLineSegment(sketch, "E32.left", {"start": v(-92.88, -6.77) * mm, "end": v(-92.88, -15.77) * mm});
            skLineSegment(sketch, "E32.right", {"start": v(-88.88, -6.77) * mm, "end": v(-88.88, -15.77) * mm});
            skLineSegment(sketch, "E33.bottom", {"start": v(95.12, -6.77) * mm, "end": v(91.12, -6.77) * mm});
            skLineSegment(sketch, "E33.top", {"start": v(95.12, -15.77) * mm, "end": v(91.12, -15.77) * mm});
            skLineSegment(sketch, "E33.left", {"start": v(95.12, -6.77) * mm, "end": v(95.12, -15.77) * mm});
            skLineSegment(sketch, "E33.right", {"start": v(91.12, -6.77) * mm, "end": v(91.12, -15.77) * mm});
            skLineSegment(sketch, "E34.0.1.0", {"start": v(-92.88, -17.77) * mm, "end": v(-88.88, -17.77) * mm});
            skLineSegment(sketch, "E34.0.1.1", {"start": v(-92.88, -17.77) * mm, "end": v(-92.88, -26.77) * mm});
            skLineSegment(sketch, "E34.0.1.2", {"start": v(-88.88, -17.77) * mm, "end": v(-88.88, -26.77) * mm});
            skLineSegment(sketch, "E34.0.1.3", {"start": v(-92.88, -26.77) * mm, "end": v(-88.88, -26.77) * mm});
            skLineSegment(sketch, "E34.0.2.0", {"start": v(-92.88, -28.77) * mm, "end": v(-88.88, -28.77) * mm});
            skLineSegment(sketch, "E34.0.2.1", {"start": v(-92.88, -28.77) * mm, "end": v(-92.88, -37.77) * mm});
            skLineSegment(sketch, "E34.0.2.2", {"start": v(-88.88, -28.77) * mm, "end": v(-88.88, -37.77) * mm});
            skLineSegment(sketch, "E34.0.2.3", {"start": v(-92.88, -37.77) * mm, "end": v(-88.88, -37.77) * mm});
            skLineSegment(sketch, "E34.0.3.0", {"start": v(-92.88, -39.77) * mm, "end": v(-88.88, -39.77) * mm});
            skLineSegment(sketch, "E34.0.3.1", {"start": v(-92.88, -39.77) * mm, "end": v(-92.88, -48.77) * mm});
            skLineSegment(sketch, "E34.0.3.2", {"start": v(-88.88, -39.77) * mm, "end": v(-88.88, -48.77) * mm});
            skLineSegment(sketch, "E34.0.3.3", {"start": v(-92.88, -48.77) * mm, "end": v(-88.88, -48.77) * mm});
            skLineSegment(sketch, "E34.0.4.0", {"start": v(-92.88, -50.77) * mm, "end": v(-88.88, -50.77) * mm});
            skLineSegment(sketch, "E34.0.4.1", {"start": v(-92.88, -50.77) * mm, "end": v(-92.88, -59.77) * mm});
            skLineSegment(sketch, "E34.0.4.2", {"start": v(-88.88, -50.77) * mm, "end": v(-88.88, -59.77) * mm});
            skLineSegment(sketch, "E34.0.4.3", {"start": v(-92.88, -59.77) * mm, "end": v(-88.88, -59.77) * mm});
            skLineSegment(sketch, "E34.0.5.0", {"start": v(-92.88, -61.77) * mm, "end": v(-88.88, -61.77) * mm});
            skLineSegment(sketch, "E34.0.5.1", {"start": v(-92.88, -61.77) * mm, "end": v(-92.88, -70.77) * mm});
            skLineSegment(sketch, "E34.0.5.2", {"start": v(-88.88, -61.77) * mm, "end": v(-88.88, -70.77) * mm});
            skLineSegment(sketch, "E34.0.5.3", {"start": v(-92.88, -70.77) * mm, "end": v(-88.88, -70.77) * mm});
            skLineSegment(sketch, "E34.0.6.0", {"start": v(-92.88, -72.77) * mm, "end": v(-88.88, -72.77) * mm});
            skLineSegment(sketch, "E34.0.6.1", {"start": v(-92.88, -72.77) * mm, "end": v(-92.88, -81.77) * mm});
            skLineSegment(sketch, "E34.0.6.2", {"start": v(-88.88, -72.77) * mm, "end": v(-88.88, -81.77) * mm});
            skLineSegment(sketch, "E34.0.6.3", {"start": v(-92.88, -81.77) * mm, "end": v(-88.88, -81.77) * mm});
            skLineSegment(sketch, "E34.direction1", {"start": v(-92.88, -6.77) * mm, "end": v(-67.88, -6.77) * mm, "construction": true});
            skLineSegment(sketch, "E34.direction2", {"start": v(-92.88, -6.77) * mm, "end": v(-92.88, -17.77) * mm, "construction": true});
            skLineSegment(sketch, "E35.MirrorCS", {"start": v(95.12, -17.77) * mm, "end": v(91.12, -17.77) * mm});
            skLineSegment(sketch, "E36.MirrorCS", {"start": v(95.12, -28.77) * mm, "end": v(91.12, -28.77) * mm});
            skLineSegment(sketch, "E37.MirrorCS", {"start": v(95.12, -26.77) * mm, "end": v(91.12, -26.77) * mm});
            skLineSegment(sketch, "E38.MirrorCS", {"start": v(95.12, -37.77) * mm, "end": v(91.12, -37.77) * mm});
            skLineSegment(sketch, "E39.MirrorCS", {"start": v(95.12, -39.77) * mm, "end": v(91.12, -39.77) * mm});
            skLineSegment(sketch, "E40.MirrorCS", {"start": v(95.12, -48.77) * mm, "end": v(91.12, -48.77) * mm});
            skLineSegment(sketch, "E41.MirrorCS", {"start": v(95.12, -50.77) * mm, "end": v(91.12, -50.77) * mm});
            skLineSegment(sketch, "E42.MirrorCS", {"start": v(95.12, -59.77) * mm, "end": v(91.12, -59.77) * mm});
            skLineSegment(sketch, "E43.MirrorCS", {"start": v(95.12, -61.77) * mm, "end": v(91.12, -61.77) * mm});
            skLineSegment(sketch, "E44.MirrorCS", {"start": v(95.12, -70.77) * mm, "end": v(91.12, -70.77) * mm});
            skLineSegment(sketch, "E45.MirrorCS", {"start": v(95.12, -72.77) * mm, "end": v(91.12, -72.77) * mm});
            skLineSegment(sketch, "E46.MirrorCS", {"start": v(95.12, -81.77) * mm, "end": v(91.12, -81.77) * mm});
            skSolve(sketch);
        }
        {
            var Q0;
            {var subQ0=sQuery(id+"F0.wireOp",EDGE,"E10.9.0.3");var subQ1=sQuery(id+"F0.wireOp",EDGE,"E9.MirrorCS");Q0=makeQuery(id+"F11.opBoolean","MERGE",FACE,{"derivedFrom":[makeQuery(id+"F8.opBoolean","MERGE",FACE,{"derivedFrom":[makeQuery(id+"F5.opBoolean","MERGE",FACE,{"derivedFrom":[makeQuery(id+"F2.opExtrude","SWEPT_FACE",FACE,{"disambiguationData":[OSD([subQ1])]}),makeQuery(id+"F2.opExtrude","SWEPT_FACE",FACE,{"disambiguationData":[OSD([sQuery(id+"F0.wireOp",EDGE,"E10.1.0.3")])]}),makeQuery(id+"F2.opExtrude","SWEPT_FACE",FACE,{"disambiguationData":[OSD([sQuery(id+"F0.wireOp",EDGE,"E10.2.0.3")])]}),makeQuery(id+"F2.opExtrude","SWEPT_FACE",FACE,{"disambiguationData":[OSD([sQuery(id+"F0.wireOp",EDGE,"E10.3.0.3")])]}),makeQuery(id+"F2.opExtrude","SWEPT_FACE",FACE,{"disambiguationData":[OSD([sQuery(id+"F0.wireOp",EDGE,"E10.4.0.3")])]}),makeQuery(id+"F2.opExtrude","SWEPT_FACE",FACE,{"disambiguationData":[OSD([sQuery(id+"F0.wireOp",EDGE,"E10.5.0.3")])]}),makeQuery(id+"F2.opExtrude","SWEPT_FACE",FACE,{"disambiguationData":[OSD([sQuery(id+"F0.wireOp",EDGE,"E10.6.0.3")])]}),makeQuery(id+"F2.opExtrude","SWEPT_FACE",FACE,{"disambiguationData":[OSD([sQuery(id+"F0.wireOp",EDGE,"E10.7.0.3")])]}),makeQuery(id+"F2.opExtrude","SWEPT_FACE",FACE,{"disambiguationData":[OSD([sQuery(id+"F0.wireOp",EDGE,"E10.8.0.3")])]}),makeQuery(id+"F2.opExtrude","SWEPT_FACE",FACE,{"disambiguationData":[OSD([subQ0])]}),makeQuery(id+"F4.opExtrude","SWEPT_FACE",FACE,{"disambiguationData":[OSD([sQuery(id+"F3.wireOp",EDGE,"E22.bottom")])]}),makeQuery(id+"F4.opExtrude","SWEPT_FACE",FACE,{"disambiguationData":[OSD([sQuery(id+"F3.wireOp",EDGE,"E23.1.0.0")])]}),makeQuery(id+"F4.opExtrude","SWEPT_FACE",FACE,{"disambiguationData":[OSD([sQuery(id+"F3.wireOp",EDGE,"E23.2.0.0")])]}),makeQuery(id+"F4.opExtrude","SWEPT_FACE",FACE,{"disambiguationData":[OSD([sQuery(id+"F3.wireOp",EDGE,"E23.3.0.0")])]}),makeQuery(id+"F4.opExtrude","SWEPT_FACE",FACE,{"disambiguationData":[OSD([sQuery(id+"F3.wireOp",EDGE,"E23.4.0.0")])]}),makeQuery(id+"F4.opExtrude","SWEPT_FACE",FACE,{"disambiguationData":[OSD([sQuery(id+"F3.wireOp",EDGE,"E23.5.0.0")])]}),makeQuery(id+"F4.opExtrude","SWEPT_FACE",FACE,{"disambiguationData":[OSD([sQuery(id+"F3.wireOp",EDGE,"E23.6.0.0")])]}),makeQuery(id+"F4.opExtrude","SWEPT_FACE",FACE,{"disambiguationData":[OSD([sQuery(id+"F3.wireOp",EDGE,"E23.7.0.0")])]}),makeQuery(id+"F4.opExtrude","SWEPT_FACE",FACE,{"disambiguationData":[OSD([sQuery(id+"F3.wireOp",EDGE,"E23.8.0.0")])]})]}),makeQuery(id+"F7.opExtrude","SWEPT_FACE",FACE,{"disambiguationData":[OSD([sQuery(id+"F0.wireOp",EDGE,"E6.MirrorCS"),subQ1])]})]}),makeQuery(id+"F10.opExtrude","SWEPT_FACE",FACE,{"disambiguationData":[OSD([sQuery(id+"F0.wireOp",EDGE,"E10.9.0.0"),subQ0])]})]});}
            var sketch = newSketch(context, id + "F13", { "sketchPlane" : qUnion([Q0])});
            skLineSegment(sketch, "E47.bottom", {"start": v(-88.88, -12.5) * mm, "end": v(-92.88, -12.5) * mm});
            skLineSegment(sketch, "E47.top", {"start": v(-88.88, -21.5) * mm, "end": v(-92.88, -21.5) * mm});
            skLineSegment(sketch, "E47.left", {"start": v(-88.88, -12.5) * mm, "end": v(-88.88, -21.5) * mm});
            skLineSegment(sketch, "E47.right", {"start": v(-92.88, -12.5) * mm, "end": v(-92.88, -21.5) * mm});
            skLineSegment(sketch, "E48.0.1.0", {"start": v(-88.88, -42.5) * mm, "end": v(-88.88, -51.5) * mm});
            skLineSegment(sketch, "E48.0.1.1", {"start": v(-88.88, -42.5) * mm, "end": v(-92.88, -42.5) * mm});
            skLineSegment(sketch, "E48.0.1.2", {"start": v(-92.88, -42.5) * mm, "end": v(-92.88, -51.5) * mm});
            skLineSegment(sketch, "E48.0.2.0", {"start": v(-88.88, -72.5) * mm, "end": v(-88.88, -81.5) * mm});
            skLineSegment(sketch, "E48.0.2.1", {"start": v(-88.88, -72.5) * mm, "end": v(-92.88, -72.5) * mm});
            skLineSegment(sketch, "E48.0.2.2", {"start": v(-92.88, -72.5) * mm, "end": v(-92.88, -81.5) * mm});
            skLineSegment(sketch, "E48.0.3.0", {"start": v(-88.88, -102.5) * mm, "end": v(-88.88, -111.5) * mm});
            skLineSegment(sketch, "E48.0.3.1", {"start": v(-88.88, -102.5) * mm, "end": v(-92.88, -102.5) * mm});
            skLineSegment(sketch, "E48.0.3.2", {"start": v(-92.88, -102.5) * mm, "end": v(-92.88, -111.5) * mm});
            skLineSegment(sketch, "E48.0.4.0", {"start": v(-88.88, -132.5) * mm, "end": v(-88.88, -141.5) * mm});
            skLineSegment(sketch, "E48.0.4.1", {"start": v(-88.88, -132.5) * mm, "end": v(-92.88, -132.5) * mm});
            skLineSegment(sketch, "E48.0.4.2", {"start": v(-92.88, -132.5) * mm, "end": v(-92.88, -141.5) * mm});
            skLineSegment(sketch, "E48.0.5.0", {"start": v(-88.88, -162.5) * mm, "end": v(-88.88, -171.5) * mm});
            skLineSegment(sketch, "E48.0.5.1", {"start": v(-88.88, -162.5) * mm, "end": v(-92.88, -162.5) * mm});
            skLineSegment(sketch, "E48.0.5.2", {"start": v(-92.88, -162.5) * mm, "end": v(-92.88, -171.5) * mm});
            skLineSegment(sketch, "E48.0.6.0", {"start": v(-88.88, -192.5) * mm, "end": v(-88.88, -201.5) * mm});
            skLineSegment(sketch, "E48.0.6.1", {"start": v(-88.88, -192.5) * mm, "end": v(-92.88, -192.5) * mm});
            skLineSegment(sketch, "E48.0.6.2", {"start": v(-92.88, -192.5) * mm, "end": v(-92.88, -201.5) * mm});
            skLineSegment(sketch, "E48.0.7.0", {"start": v(-88.88, -222.5) * mm, "end": v(-88.88, -231.5) * mm});
            skLineSegment(sketch, "E48.0.7.1", {"start": v(-88.88, -222.5) * mm, "end": v(-92.88, -222.5) * mm});
            skLineSegment(sketch, "E48.0.7.2", {"start": v(-92.88, -222.5) * mm, "end": v(-92.88, -231.5) * mm});
            skLineSegment(sketch, "E48.0.8.0", {"start": v(-88.88, -252.5) * mm, "end": v(-88.88, -261.5) * mm});
            skLineSegment(sketch, "E48.0.8.1", {"start": v(-88.88, -252.5) * mm, "end": v(-92.88, -252.5) * mm});
            skLineSegment(sketch, "E48.0.8.2", {"start": v(-92.88, -252.5) * mm, "end": v(-92.88, -261.5) * mm});
            skLineSegment(sketch, "E48.0.9.0", {"start": v(-88.88, -282.5) * mm, "end": v(-88.88, -291.5) * mm});
            skLineSegment(sketch, "E48.0.9.1", {"start": v(-88.88, -282.5) * mm, "end": v(-92.88, -282.5) * mm});
            skLineSegment(sketch, "E48.0.9.2", {"start": v(-92.88, -282.5) * mm, "end": v(-92.88, -291.5) * mm});
            skLineSegment(sketch, "E48.direction1", {"start": v(-88.88, -21.5) * mm, "end": v(-63.88, -21.5) * mm, "construction": true});
            skLineSegment(sketch, "E48.direction2", {"start": v(-88.88, -21.5) * mm, "end": v(-88.88, -51.5) * mm, "construction": true});
            skLineSegment(sketch, "E49.0.1.0", {"start": v(-88.88, -51.5) * mm, "end": v(-92.88, -51.5) * mm});
            skLineSegment(sketch, "E49.0.2.0", {"start": v(-88.88, -81.5) * mm, "end": v(-92.88, -81.5) * mm});
            skLineSegment(sketch, "E49.0.3.0", {"start": v(-88.88, -111.5) * mm, "end": v(-92.88, -111.5) * mm});
            skLineSegment(sketch, "E49.0.4.0", {"start": v(-88.88, -141.5) * mm, "end": v(-92.88, -141.5) * mm});
            skLineSegment(sketch, "E49.0.5.0", {"start": v(-88.88, -171.5) * mm, "end": v(-92.88, -171.5) * mm});
            skLineSegment(sketch, "E49.0.6.0", {"start": v(-88.88, -201.5) * mm, "end": v(-92.88, -201.5) * mm});
            skLineSegment(sketch, "E49.0.7.0", {"start": v(-88.88, -231.5) * mm, "end": v(-92.88, -231.5) * mm});
            skLineSegment(sketch, "E49.0.8.0", {"start": v(-88.88, -261.5) * mm, "end": v(-92.88, -261.5) * mm});
            skLineSegment(sketch, "E49.0.9.0", {"start": v(-88.88, -291.5) * mm, "end": v(-92.88, -291.5) * mm});
            skLineSegment(sketch, "E49.direction1", {"start": v(-92.88, -21.5) * mm, "end": v(-67.88, -21.5) * mm, "construction": true});
            skLineSegment(sketch, "E49.direction2", {"start": v(-92.88, -21.5) * mm, "end": v(-92.88, -51.5) * mm, "construction": true});
            skPoint(sketch, "E50.startSnap0", {"position": v(1.12, -296) * mm});
            skPoint(sketch, "E50.endSnap0", {"position": v(1.12, -296) * mm});
            skLineSegment(sketch, "E51", {"start": v(1.12, -296) * mm, "end": v(1.12, -4) * mm, "construction": true});
            skLineSegment(sketch, "E52.MirrorCS", {"start": v(91.12, -282.5) * mm, "end": v(91.12, -291.5) * mm});
            skLineSegment(sketch, "E53.MirrorCS", {"start": v(91.12, -291.5) * mm, "end": v(95.12, -291.5) * mm});
            skLineSegment(sketch, "E54.MirrorCS", {"start": v(95.12, -282.5) * mm, "end": v(95.12, -291.5) * mm});
            skLineSegment(sketch, "E55.MirrorCS", {"start": v(91.12, -282.5) * mm, "end": v(95.12, -282.5) * mm});
            skLineSegment(sketch, "E56.0.1.0", {"start": v(91.12, -252.5) * mm, "end": v(95.12, -252.5) * mm});
            skLineSegment(sketch, "E56.0.1.1", {"start": v(91.12, -252.5) * mm, "end": v(91.12, -261.5) * mm});
            skLineSegment(sketch, "E56.0.1.2", {"start": v(91.12, -261.5) * mm, "end": v(95.12, -261.5) * mm});
            skLineSegment(sketch, "E56.0.1.3", {"start": v(95.12, -252.5) * mm, "end": v(95.12, -261.5) * mm});
            skLineSegment(sketch, "E56.0.2.0", {"start": v(91.12, -222.5) * mm, "end": v(95.12, -222.5) * mm});
            skLineSegment(sketch, "E56.0.2.1", {"start": v(91.12, -222.5) * mm, "end": v(91.12, -231.5) * mm});
            skLineSegment(sketch, "E56.0.2.2", {"start": v(91.12, -231.5) * mm, "end": v(95.12, -231.5) * mm});
            skLineSegment(sketch, "E56.0.2.3", {"start": v(95.12, -222.5) * mm, "end": v(95.12, -231.5) * mm});
            skLineSegment(sketch, "E56.0.3.0", {"start": v(91.12, -192.5) * mm, "end": v(95.12, -192.5) * mm});
            skLineSegment(sketch, "E56.0.3.1", {"start": v(91.12, -192.5) * mm, "end": v(91.12, -201.5) * mm});
            skLineSegment(sketch, "E56.0.3.2", {"start": v(91.12, -201.5) * mm, "end": v(95.12, -201.5) * mm});
            skLineSegment(sketch, "E56.0.3.3", {"start": v(95.12, -192.5) * mm, "end": v(95.12, -201.5) * mm});
            skLineSegment(sketch, "E56.0.4.0", {"start": v(91.12, -162.5) * mm, "end": v(95.12, -162.5) * mm});
            skLineSegment(sketch, "E56.0.4.1", {"start": v(91.12, -162.5) * mm, "end": v(91.12, -171.5) * mm});
            skLineSegment(sketch, "E56.0.4.2", {"start": v(91.12, -171.5) * mm, "end": v(95.12, -171.5) * mm});
            skLineSegment(sketch, "E56.0.4.3", {"start": v(95.12, -162.5) * mm, "end": v(95.12, -171.5) * mm});
            skLineSegment(sketch, "E56.0.5.0", {"start": v(91.12, -132.5) * mm, "end": v(95.12, -132.5) * mm});
            skLineSegment(sketch, "E56.0.5.1", {"start": v(91.12, -132.5) * mm, "end": v(91.12, -141.5) * mm});
            skLineSegment(sketch, "E56.0.5.2", {"start": v(91.12, -141.5) * mm, "end": v(95.12, -141.5) * mm});
            skLineSegment(sketch, "E56.0.5.3", {"start": v(95.12, -132.5) * mm, "end": v(95.12, -141.5) * mm});
            skLineSegment(sketch, "E56.0.6.0", {"start": v(91.12, -102.5) * mm, "end": v(95.12, -102.5) * mm});
            skLineSegment(sketch, "E56.0.6.1", {"start": v(91.12, -102.5) * mm, "end": v(91.12, -111.5) * mm});
            skLineSegment(sketch, "E56.0.6.2", {"start": v(91.12, -111.5) * mm, "end": v(95.12, -111.5) * mm});
            skLineSegment(sketch, "E56.0.6.3", {"start": v(95.12, -102.5) * mm, "end": v(95.12, -111.5) * mm});
            skLineSegment(sketch, "E56.0.7.0", {"start": v(91.12, -72.5) * mm, "end": v(95.12, -72.5) * mm});
            skLineSegment(sketch, "E56.0.7.1", {"start": v(91.12, -72.5) * mm, "end": v(91.12, -81.5) * mm});
            skLineSegment(sketch, "E56.0.7.2", {"start": v(91.12, -81.5) * mm, "end": v(95.12, -81.5) * mm});
            skLineSegment(sketch, "E56.0.7.3", {"start": v(95.12, -72.5) * mm, "end": v(95.12, -81.5) * mm});
            skLineSegment(sketch, "E56.0.8.0", {"start": v(91.12, -42.5) * mm, "end": v(95.12, -42.5) * mm});
            skLineSegment(sketch, "E56.0.8.1", {"start": v(91.12, -42.5) * mm, "end": v(91.12, -51.5) * mm});
            skLineSegment(sketch, "E56.0.8.2", {"start": v(91.12, -51.5) * mm, "end": v(95.12, -51.5) * mm});
            skLineSegment(sketch, "E56.0.8.3", {"start": v(95.12, -42.5) * mm, "end": v(95.12, -51.5) * mm});
            skLineSegment(sketch, "E56.0.9.0", {"start": v(91.12, -12.5) * mm, "end": v(95.12, -12.5) * mm});
            skLineSegment(sketch, "E56.0.9.1", {"start": v(91.12, -12.5) * mm, "end": v(91.12, -21.5) * mm});
            skLineSegment(sketch, "E56.0.9.2", {"start": v(91.12, -21.5) * mm, "end": v(95.12, -21.5) * mm});
            skLineSegment(sketch, "E56.0.9.3", {"start": v(95.12, -12.5) * mm, "end": v(95.12, -21.5) * mm});
            skLineSegment(sketch, "E56.direction1", {"start": v(91.12, -282.5) * mm, "end": v(116.12, -282.5) * mm, "construction": true});
            skLineSegment(sketch, "E56.direction2", {"start": v(91.12, -282.5) * mm, "end": v(91.12, -252.5) * mm, "construction": true});
            skSolve(sketch);
        }
        {
            var Q0;
            Q0=makeQuery(id+"F13.imprint","IMPRINT",FACE,{"disambiguationData":[TD([[makeQuery(id+"F13.imprint","IMPRINT",EDGE,{"derivedFrom":sQuery(id+"F13.wireOp",EDGE,"E47.bottom")}),1.0]])]});
            var Q1;
            Q1=makeQuery(id+"F13.imprint","IMPRINT",FACE,{"disambiguationData":[TD([[makeQuery(id+"F13.imprint","IMPRINT",EDGE,{"derivedFrom":sQuery(id+"F13.wireOp",EDGE,"E48.0.1.0")}),-1.0]])]});
            var Q2;
            Q2=makeQuery(id+"F13.imprint","IMPRINT",FACE,{"disambiguationData":[TD([[makeQuery(id+"F13.imprint","IMPRINT",EDGE,{"derivedFrom":sQuery(id+"F13.wireOp",EDGE,"E48.0.2.0")}),-1.0]])]});
            var Q3;
            Q3=makeQuery(id+"F13.imprint","IMPRINT",FACE,{"disambiguationData":[TD([[makeQuery(id+"F13.imprint","IMPRINT",EDGE,{"derivedFrom":sQuery(id+"F13.wireOp",EDGE,"E48.0.3.0")}),-1.0]])]});
            var Q4;
            Q4=makeQuery(id+"F13.imprint","IMPRINT",FACE,{"disambiguationData":[TD([[makeQuery(id+"F13.imprint","IMPRINT",EDGE,{"derivedFrom":sQuery(id+"F13.wireOp",EDGE,"E48.0.4.0")}),-1.0]])]});
            var Q5;
            Q5=makeQuery(id+"F13.imprint","IMPRINT",FACE,{"disambiguationData":[TD([[makeQuery(id+"F13.imprint","IMPRINT",EDGE,{"derivedFrom":sQuery(id+"F13.wireOp",EDGE,"E48.0.5.0")}),-1.0]])]});
            var Q6;
            Q6=makeQuery(id+"F13.imprint","IMPRINT",FACE,{"disambiguationData":[TD([[makeQuery(id+"F13.imprint","IMPRINT",EDGE,{"derivedFrom":sQuery(id+"F13.wireOp",EDGE,"E48.0.6.0")}),-1.0]])]});
            var Q7;
            Q7=makeQuery(id+"F13.imprint","IMPRINT",FACE,{"disambiguationData":[TD([[makeQuery(id+"F13.imprint","IMPRINT",EDGE,{"derivedFrom":sQuery(id+"F13.wireOp",EDGE,"E48.0.7.0")}),-1.0]])]});
            var Q8;
            Q8=makeQuery(id+"F13.imprint","IMPRINT",FACE,{"disambiguationData":[TD([[makeQuery(id+"F13.imprint","IMPRINT",EDGE,{"derivedFrom":sQuery(id+"F13.wireOp",EDGE,"E48.0.8.0")}),-1.0]])]});
            var Q9;
            Q9=makeQuery(id+"F13.imprint","IMPRINT",FACE,{"disambiguationData":[TD([[makeQuery(id+"F13.imprint","IMPRINT",EDGE,{"derivedFrom":sQuery(id+"F13.wireOp",EDGE,"E48.0.9.0")}),-1.0]])]});
            var Q10;
            Q10=makeQuery(id+"F13.imprint","IMPRINT",FACE,{"disambiguationData":[TD([[makeQuery(id+"F13.imprint","IMPRINT",EDGE,{"derivedFrom":sQuery(id+"F13.wireOp",EDGE,"E52.MirrorCS")}),1.0]])]});
            var Q11;
            Q11=makeQuery(id+"F13.imprint","IMPRINT",FACE,{"disambiguationData":[TD([[makeQuery(id+"F13.imprint","IMPRINT",EDGE,{"derivedFrom":sQuery(id+"F13.wireOp",EDGE,"E56.0.1.0")}),-1.0]])]});
            var Q12;
            Q12=makeQuery(id+"F13.imprint","IMPRINT",FACE,{"disambiguationData":[TD([[makeQuery(id+"F13.imprint","IMPRINT",EDGE,{"derivedFrom":sQuery(id+"F13.wireOp",EDGE,"E56.0.2.0")}),-1.0]])]});
            var Q13;
            Q13=makeQuery(id+"F13.imprint","IMPRINT",FACE,{"disambiguationData":[TD([[makeQuery(id+"F13.imprint","IMPRINT",EDGE,{"derivedFrom":sQuery(id+"F13.wireOp",EDGE,"E56.0.3.0")}),-1.0]])]});
            var Q14;
            Q14=makeQuery(id+"F13.imprint","IMPRINT",FACE,{"disambiguationData":[TD([[makeQuery(id+"F13.imprint","IMPRINT",EDGE,{"derivedFrom":sQuery(id+"F13.wireOp",EDGE,"E56.0.4.0")}),-1.0]])]});
            var Q15;
            Q15=makeQuery(id+"F13.imprint","IMPRINT",FACE,{"disambiguationData":[TD([[makeQuery(id+"F13.imprint","IMPRINT",EDGE,{"derivedFrom":sQuery(id+"F13.wireOp",EDGE,"E56.0.5.0")}),-1.0]])]});
            var Q16;
            Q16=makeQuery(id+"F13.imprint","IMPRINT",FACE,{"disambiguationData":[TD([[makeQuery(id+"F13.imprint","IMPRINT",EDGE,{"derivedFrom":sQuery(id+"F13.wireOp",EDGE,"E56.0.6.0")}),-1.0]])]});
            var Q17;
            Q17=makeQuery(id+"F13.imprint","IMPRINT",FACE,{"disambiguationData":[TD([[makeQuery(id+"F13.imprint","IMPRINT",EDGE,{"derivedFrom":sQuery(id+"F13.wireOp",EDGE,"E56.0.7.0")}),-1.0]])]});
            var Q18;
            Q18=makeQuery(id+"F13.imprint","IMPRINT",FACE,{"disambiguationData":[TD([[makeQuery(id+"F13.imprint","IMPRINT",EDGE,{"derivedFrom":sQuery(id+"F13.wireOp",EDGE,"E56.0.8.0")}),-1.0]])]});
            var Q19;
            Q19=makeQuery(id+"F13.imprint","IMPRINT",FACE,{"disambiguationData":[TD([[makeQuery(id+"F13.imprint","IMPRINT",EDGE,{"derivedFrom":sQuery(id+"F13.wireOp",EDGE,"E56.0.9.0")}),-1.0]])]});
            extrude(context, id + "F14", {"entities" : qUnion([Q0, Q1, Q2, Q3, Q4, Q5, Q6, Q7, Q8, Q9, Q10, Q11, Q12, Q13, Q14, Q15, Q16, Q17, Q18, Q19]), "operationType" : NewBodyOperationType.REMOVE, "oppositeDirection" : true, "depth" : 4 * mm});
        }
        {
            var Q0;
            {var subQ32=sQuery(id+"F12.wireOp",EDGE,"E29.top");Q0=makeQuery(id+"F12.imprint","IMPRINT",FACE,{"disambiguationData":[TD([[makeQuery(id+"F12.imprint","IMPRINT",EDGE,{"derivedFrom":subQ32}),-1.0]])]});}
            var sketch = newSketch(context, id + "F15", { "sketchPlane" : qUnion([Q0])});
            skLineSegment(sketch, "E57.bottom", {"start": v(-92.88, -6.77) * mm, "end": v(-88.88, -6.77) * mm});
            skLineSegment(sketch, "E57.top", {"start": v(-92.88, -81.77) * mm, "end": v(-88.88, -81.77) * mm});
            skLineSegment(sketch, "E57.left", {"start": v(-92.88, -6.77) * mm, "end": v(-92.88, -81.77) * mm});
            skLineSegment(sketch, "E57.right", {"start": v(-88.88, -6.77) * mm, "end": v(-88.88, -81.77) * mm});
            skLineSegment(sketch, "E58.top", {"start": v(-92.88, -15.77) * mm, "end": v(-88.88, -15.77) * mm});
            skLineSegment(sketch, "E58.left", {"start": v(-92.88, -6.77) * mm, "end": v(-92.88, -15.77) * mm});
            skLineSegment(sketch, "E58.right", {"start": v(-88.88, -6.77) * mm, "end": v(-88.88, -15.77) * mm});
            skLineSegment(sketch, "E59.0.1.0", {"start": v(-92.88, -17.77) * mm, "end": v(-88.88, -17.77) * mm});
            skLineSegment(sketch, "E59.0.1.1", {"start": v(-92.88, -17.77) * mm, "end": v(-92.88, -26.77) * mm});
            skLineSegment(sketch, "E59.0.1.2", {"start": v(-92.88, -26.77) * mm, "end": v(-88.88, -26.77) * mm});
            skLineSegment(sketch, "E59.0.1.3", {"start": v(-88.88, -17.77) * mm, "end": v(-88.88, -26.77) * mm});
            skLineSegment(sketch, "E59.0.2.0", {"start": v(-92.88, -28.77) * mm, "end": v(-88.88, -28.77) * mm});
            skLineSegment(sketch, "E59.0.2.1", {"start": v(-92.88, -28.77) * mm, "end": v(-92.88, -37.77) * mm});
            skLineSegment(sketch, "E59.0.2.2", {"start": v(-92.88, -37.77) * mm, "end": v(-88.88, -37.77) * mm});
            skLineSegment(sketch, "E59.0.2.3", {"start": v(-88.88, -28.77) * mm, "end": v(-88.88, -37.77) * mm});
            skLineSegment(sketch, "E59.0.3.0", {"start": v(-92.88, -39.77) * mm, "end": v(-88.88, -39.77) * mm});
            skLineSegment(sketch, "E59.0.3.1", {"start": v(-92.88, -39.77) * mm, "end": v(-92.88, -48.77) * mm});
            skLineSegment(sketch, "E59.0.3.2", {"start": v(-92.88, -48.77) * mm, "end": v(-88.88, -48.77) * mm});
            skLineSegment(sketch, "E59.0.3.3", {"start": v(-88.88, -39.77) * mm, "end": v(-88.88, -48.77) * mm});
            skLineSegment(sketch, "E59.0.4.0", {"start": v(-92.88, -50.77) * mm, "end": v(-88.88, -50.77) * mm});
            skLineSegment(sketch, "E59.0.4.1", {"start": v(-92.88, -50.77) * mm, "end": v(-92.88, -59.77) * mm});
            skLineSegment(sketch, "E59.0.4.2", {"start": v(-92.88, -59.77) * mm, "end": v(-88.88, -59.77) * mm});
            skLineSegment(sketch, "E59.0.4.3", {"start": v(-88.88, -50.77) * mm, "end": v(-88.88, -59.77) * mm});
            skLineSegment(sketch, "E59.0.5.0", {"start": v(-92.88, -61.77) * mm, "end": v(-88.88, -61.77) * mm});
            skLineSegment(sketch, "E59.0.5.1", {"start": v(-92.88, -61.77) * mm, "end": v(-92.88, -70.77) * mm});
            skLineSegment(sketch, "E59.0.5.2", {"start": v(-92.88, -70.77) * mm, "end": v(-88.88, -70.77) * mm});
            skLineSegment(sketch, "E59.0.5.3", {"start": v(-88.88, -61.77) * mm, "end": v(-88.88, -70.77) * mm});
            skLineSegment(sketch, "E59.0.6.0", {"start": v(-92.88, -72.77) * mm, "end": v(-88.88, -72.77) * mm});
            skLineSegment(sketch, "E59.0.6.1", {"start": v(-92.88, -72.77) * mm, "end": v(-92.88, -81.77) * mm});
            skLineSegment(sketch, "E59.0.6.3", {"start": v(-88.88, -72.77) * mm, "end": v(-88.88, -81.77) * mm});
            skLineSegment(sketch, "E59.direction1", {"start": v(-92.88, -6.77) * mm, "end": v(-67.88, -6.77) * mm, "construction": true});
            skLineSegment(sketch, "E59.direction2", {"start": v(-92.88, -6.77) * mm, "end": v(-92.88, -17.77) * mm, "construction": true});
            skLineSegment(sketch, "E60.MirrorCS", {"start": v(91.12, -6.77) * mm, "end": v(91.12, -15.77) * mm});
            skLineSegment(sketch, "E61.MirrorCS", {"start": v(95.12, -6.77) * mm, "end": v(95.12, -81.77) * mm});
            skLineSegment(sketch, "E62.MirrorCS", {"start": v(91.12, -6.77) * mm, "end": v(91.12, -81.77) * mm});
            skLineSegment(sketch, "E63.MirrorCS", {"start": v(95.12, -28.77) * mm, "end": v(91.12, -28.77) * mm});
            skLineSegment(sketch, "E64.MirrorCS", {"start": v(95.12, -26.77) * mm, "end": v(91.12, -26.77) * mm});
            skLineSegment(sketch, "E65.MirrorCS", {"start": v(95.12, -17.77) * mm, "end": v(91.12, -17.77) * mm});
            skLineSegment(sketch, "E66.MirrorCS", {"start": v(95.12, -15.77) * mm, "end": v(91.12, -15.77) * mm});
            skLineSegment(sketch, "E67.MirrorCS", {"start": v(95.12, -39.77) * mm, "end": v(91.12, -39.77) * mm});
            skLineSegment(sketch, "E68.MirrorCS", {"start": v(95.12, -48.77) * mm, "end": v(91.12, -48.77) * mm});
            skLineSegment(sketch, "E69.MirrorCS", {"start": v(95.12, -50.77) * mm, "end": v(91.12, -50.77) * mm});
            skLineSegment(sketch, "E70.MirrorCS", {"start": v(95.12, -59.77) * mm, "end": v(91.12, -59.77) * mm});
            skLineSegment(sketch, "E71.MirrorCS", {"start": v(95.12, -61.77) * mm, "end": v(91.12, -61.77) * mm});
            skLineSegment(sketch, "E72.MirrorCS", {"start": v(95.12, -70.77) * mm, "end": v(91.12, -70.77) * mm});
            skLineSegment(sketch, "E73.MirrorCS", {"start": v(95.12, -72.77) * mm, "end": v(91.12, -72.77) * mm});
            skLineSegment(sketch, "E74.MirrorCS", {"start": v(95.12, -37.77) * mm, "end": v(91.12, -37.77) * mm});
            skLineSegment(sketch, "E75.MirrorCS", {"start": v(95.12, -6.77) * mm, "end": v(70.12, -6.77) * mm, "construction": true});
            skLineSegment(sketch, "E76", {"start": v(91.12, -6.77) * mm, "end": v(95.12, -6.77) * mm});
            skLineSegment(sketch, "E77.bottom", {"start": v(91.12, -81.77) * mm, "end": v(95.12, -81.77) * mm});
            skLineSegment(sketch, "E77.top", {"start": v(91.12, -84.77) * mm, "end": v(95.12, -84.77) * mm});
            skLineSegment(sketch, "E77.left", {"start": v(91.12, -81.77) * mm, "end": v(91.12, -84.77) * mm});
            skLineSegment(sketch, "E77.right", {"start": v(95.12, -81.77) * mm, "end": v(95.12, -84.77) * mm});
            skSolve(sketch);
        }
        {
            var Q0;
            Q0=makeQuery(id+"F0.imprint","IMPRINT",FACE,{"disambiguationData":[TD([[makeQuery(id+"F0.imprint","IMPRINT",EDGE,{"derivedFrom":sQuery(id+"F0.wireOp",EDGE,"E12.0.6.0")}),1.0]])]});
            var Q1;
            Q1=makeQuery(id+"F0.imprint","IMPRINT",FACE,{"disambiguationData":[TD([[makeQuery(id+"F0.imprint","IMPRINT",EDGE,{"derivedFrom":sQuery(id+"F0.wireOp",EDGE,"E12.0.5.0")}),1.0]])]});
            var Q2;
            Q2=makeQuery(id+"F0.imprint","IMPRINT",FACE,{"disambiguationData":[TD([[makeQuery(id+"F0.imprint","IMPRINT",EDGE,{"derivedFrom":sQuery(id+"F0.wireOp",EDGE,"E12.0.4.0")}),1.0]])]});
            var Q3;
            Q3=makeQuery(id+"F0.imprint","IMPRINT",FACE,{"disambiguationData":[TD([[makeQuery(id+"F0.imprint","IMPRINT",EDGE,{"derivedFrom":sQuery(id+"F0.wireOp",EDGE,"E12.0.3.0")}),1.0]])]});
            var Q4;
            Q4=makeQuery(id+"F0.imprint","IMPRINT",FACE,{"disambiguationData":[TD([[makeQuery(id+"F0.imprint","IMPRINT",EDGE,{"derivedFrom":sQuery(id+"F0.wireOp",EDGE,"E12.0.2.0")}),1.0]])]});
            var Q5;
            Q5=makeQuery(id+"F0.imprint","IMPRINT",FACE,{"disambiguationData":[TD([[makeQuery(id+"F0.imprint","IMPRINT",EDGE,{"derivedFrom":sQuery(id+"F0.wireOp",EDGE,"E12.0.1.0")}),1.0]])]});
            var Q6;
            Q6=makeQuery(id+"F0.imprint","IMPRINT",FACE,{"disambiguationData":[TD([[makeQuery(id+"F0.imprint","IMPRINT",EDGE,{"derivedFrom":sQuery(id+"F0.wireOp",EDGE,"E11.bottom")}),-1.0]])]});
            var Q7;
            Q7=makeQuery(id+"F0.imprint","IMPRINT",FACE,{"disambiguationData":[TD([[makeQuery(id+"F0.imprint","IMPRINT",EDGE,{"derivedFrom":sQuery(id+"F0.wireOp",EDGE,"E19.0.6.0")}),-1.0]])]});
            var Q8;
            Q8=makeQuery(id+"F0.imprint","IMPRINT",FACE,{"disambiguationData":[TD([[makeQuery(id+"F0.imprint","IMPRINT",EDGE,{"derivedFrom":sQuery(id+"F0.wireOp",EDGE,"E19.0.5.0")}),-1.0]])]});
            var Q9;
            Q9=makeQuery(id+"F0.imprint","IMPRINT",FACE,{"disambiguationData":[TD([[makeQuery(id+"F0.imprint","IMPRINT",EDGE,{"derivedFrom":sQuery(id+"F0.wireOp",EDGE,"E19.0.4.0")}),-1.0]])]});
            var Q10;
            Q10=makeQuery(id+"F0.imprint","IMPRINT",FACE,{"disambiguationData":[TD([[makeQuery(id+"F0.imprint","IMPRINT",EDGE,{"derivedFrom":sQuery(id+"F0.wireOp",EDGE,"E19.0.3.0")}),-1.0]])]});
            var Q11;
            Q11=makeQuery(id+"F0.imprint","IMPRINT",FACE,{"disambiguationData":[TD([[makeQuery(id+"F0.imprint","IMPRINT",EDGE,{"derivedFrom":sQuery(id+"F0.wireOp",EDGE,"E19.0.2.0")}),-1.0]])]});
            var Q12;
            Q12=makeQuery(id+"F0.imprint","IMPRINT",FACE,{"disambiguationData":[TD([[makeQuery(id+"F0.imprint","IMPRINT",EDGE,{"derivedFrom":sQuery(id+"F0.wireOp",EDGE,"E19.0.1.0")}),-1.0]])]});
            var Q13;
            Q13=makeQuery(id+"F0.imprint","IMPRINT",FACE,{"disambiguationData":[TD([[makeQuery(id+"F0.imprint","IMPRINT",EDGE,{"derivedFrom":sQuery(id+"F0.wireOp",EDGE,"E14.MirrorCS")}),1.0]])]});
            extrude(context, id + "F16", {"entities" : qUnion([Q0, Q1, Q2, Q3, Q4, Q5, Q6, Q7, Q8, Q9, Q10, Q11, Q12, Q13]), "depth" : 300 * mm});
        }
        {
            var Q0;
            {var subQ0=sQuery(id+"F12.wireOp",EDGE,"E29.bottom");Q0=makeQuery(id+"F12.imprint","IMPRINT",FACE,{"disambiguationData":[TD([[makeQuery(id+"F12.imprint","IMPRINT",EDGE,{"derivedFrom":subQ0}),-1.0]])]});}
            var Q1;
            {var subQ2=sQuery(id+"F12.wireOp",EDGE,"E32.top");Q1=makeQuery(id+"F12.imprint","IMPRINT",FACE,{"disambiguationData":[TD([[makeQuery(id+"F12.imprint","IMPRINT",EDGE,{"derivedFrom":subQ2}),1.0]])]});}
            var Q2;
            {var subQ2=sQuery(id+"F12.wireOp",EDGE,"E34.0.1.3");Q2=makeQuery(id+"F12.imprint","IMPRINT",FACE,{"disambiguationData":[TD([[makeQuery(id+"F12.imprint","IMPRINT",EDGE,{"derivedFrom":subQ2}),1.0]])]});}
            var Q3;
            {var subQ2=sQuery(id+"F12.wireOp",EDGE,"E34.0.2.3");Q3=makeQuery(id+"F12.imprint","IMPRINT",FACE,{"disambiguationData":[TD([[makeQuery(id+"F12.imprint","IMPRINT",EDGE,{"derivedFrom":subQ2}),1.0]])]});}
            var Q4;
            {var subQ2=sQuery(id+"F12.wireOp",EDGE,"E34.0.3.3");Q4=makeQuery(id+"F12.imprint","IMPRINT",FACE,{"disambiguationData":[TD([[makeQuery(id+"F12.imprint","IMPRINT",EDGE,{"derivedFrom":subQ2}),1.0]])]});}
            var Q5;
            {var subQ2=sQuery(id+"F12.wireOp",EDGE,"E34.0.4.3");Q5=makeQuery(id+"F12.imprint","IMPRINT",FACE,{"disambiguationData":[TD([[makeQuery(id+"F12.imprint","IMPRINT",EDGE,{"derivedFrom":subQ2}),1.0]])]});}
            var Q6;
            {var subQ2=sQuery(id+"F12.wireOp",EDGE,"E34.0.5.3");Q6=makeQuery(id+"F12.imprint","IMPRINT",FACE,{"disambiguationData":[TD([[makeQuery(id+"F12.imprint","IMPRINT",EDGE,{"derivedFrom":subQ2}),1.0]])]});}
            var Q7;
            {var subQ0=sQuery(id+"F12.wireOp",EDGE,"E29.top");Q7=makeQuery(id+"F12.imprint","IMPRINT",FACE,{"disambiguationData":[TD([[makeQuery(id+"F12.imprint","IMPRINT",EDGE,{"derivedFrom":subQ0}),1.0]])]});}
            var Q8;
            {var subQ0=sQuery(id+"F12.wireOp",EDGE,"E33.bottom");Q8=makeQuery(id+"F12.imprint","IMPRINT",FACE,{"disambiguationData":[TD([[makeQuery(id+"F12.imprint","IMPRINT",EDGE,{"derivedFrom":subQ0}),1.0]])]});}
            var Q9;
            {var subQ2=sQuery(id+"F12.wireOp",EDGE,"E33.top");Q9=makeQuery(id+"F12.imprint","IMPRINT",FACE,{"disambiguationData":[TD([[makeQuery(id+"F12.imprint","IMPRINT",EDGE,{"derivedFrom":subQ2}),-1.0]])]});}
            var Q10;
            {var subQ0=sQuery(id+"F12.wireOp",EDGE,"E36.MirrorCS");Q10=makeQuery(id+"F12.imprint","IMPRINT",FACE,{"disambiguationData":[TD([[makeQuery(id+"F12.imprint","IMPRINT",EDGE,{"derivedFrom":subQ0}),1.0]])]});}
            var Q11;
            {var subQ0=sQuery(id+"F15.wireOp",EDGE,"E67.MirrorCS");Q11=makeQuery(id+"F15.imprint","IMPRINT",FACE,{"disambiguationData":[TD([[makeQuery(id+"F15.imprint","IMPRINT",EDGE,{"derivedFrom":subQ0}),-1.0]])]});}
            var Q12;
            {var subQ2=sQuery(id+"F15.wireOp",EDGE,"E68.MirrorCS");Q12=makeQuery(id+"F15.imprint","IMPRINT",FACE,{"disambiguationData":[TD([[makeQuery(id+"F15.imprint","IMPRINT",EDGE,{"derivedFrom":subQ2}),1.0]])]});}
            var Q13;
            {var subQ2=sQuery(id+"F12.wireOp",EDGE,"E42.MirrorCS");Q13=makeQuery(id+"F12.imprint","IMPRINT",FACE,{"disambiguationData":[TD([[makeQuery(id+"F12.imprint","IMPRINT",EDGE,{"derivedFrom":subQ2}),-1.0]])]});}
            var Q14;
            {var subQ2=sQuery(id+"F12.wireOp",EDGE,"E44.MirrorCS");Q14=makeQuery(id+"F12.imprint","IMPRINT",FACE,{"disambiguationData":[TD([[makeQuery(id+"F12.imprint","IMPRINT",EDGE,{"derivedFrom":subQ2}),-1.0]])]});}
            var Q15;
            Q15=makeQuery(id+"F15.imprint","IMPRINT",FACE,{"disambiguationData":[TD([[makeQuery(id+"F15.imprint","IMPRINT",EDGE,{"derivedFrom":sQuery(id+"F15.wireOp",EDGE,"E77.bottom")}),-1.0]])]});
            extrude(context, id + "F17", {"entities" : qUnion([Q0, Q1, Q2, Q3, Q4, Q5, Q6, Q7, Q8, Q9, Q10, Q11, Q12, Q13, Q14, Q15]), "depth" : 292 * mm});
        }
        {
            var Q0;
            Q0=makeQuery(id+"F16.opExtrude","SWEPT_BODY",BODY,{"disambiguationData":[OSD([sQuery(id+"F0.wireOp",EDGE,"E14.MirrorCS"),sQuery(id+"F0.wireOp",EDGE,"E15.MirrorCS"),sQuery(id+"F0.wireOp",EDGE,"E16.MirrorCS"),sQuery(id+"F0.wireOp",EDGE,"E18.MirrorCS")])]});
            deleteBodies(context, id + "F18", {"entities" : qUnion([Q0])});
        }
        {
            var Q0;
            Q0=makeQuery(id+"F13.imprint","IMPRINT",FACE,{"disambiguationData":[TD([[makeQuery(id+"F13.imprint","IMPRINT",EDGE,{"derivedFrom":sQuery(id+"F13.wireOp",EDGE,"E47.bottom")}),1.0]])]});
            var Q1;
            Q1=makeQuery(id+"F13.imprint","IMPRINT",FACE,{"disambiguationData":[TD([[makeQuery(id+"F13.imprint","IMPRINT",EDGE,{"derivedFrom":sQuery(id+"F13.wireOp",EDGE,"E48.0.1.0")}),-1.0]])]});
            var Q2;
            Q2=makeQuery(id+"F13.imprint","IMPRINT",FACE,{"disambiguationData":[TD([[makeQuery(id+"F13.imprint","IMPRINT",EDGE,{"derivedFrom":sQuery(id+"F13.wireOp",EDGE,"E48.0.2.0")}),-1.0]])]});
            var Q3;
            Q3=makeQuery(id+"F13.imprint","IMPRINT",FACE,{"disambiguationData":[TD([[makeQuery(id+"F13.imprint","IMPRINT",EDGE,{"derivedFrom":sQuery(id+"F13.wireOp",EDGE,"E48.0.3.0")}),-1.0]])]});
            var Q4;
            Q4=makeQuery(id+"F13.imprint","IMPRINT",FACE,{"disambiguationData":[TD([[makeQuery(id+"F13.imprint","IMPRINT",EDGE,{"derivedFrom":sQuery(id+"F13.wireOp",EDGE,"E48.0.5.0")}),-1.0]])]});
            var Q5;
            Q5=makeQuery(id+"F13.imprint","IMPRINT",FACE,{"disambiguationData":[TD([[makeQuery(id+"F13.imprint","IMPRINT",EDGE,{"derivedFrom":sQuery(id+"F13.wireOp",EDGE,"E48.0.7.0")}),-1.0]])]});
            var Q6;
            Q6=makeQuery(id+"F13.imprint","IMPRINT",FACE,{"disambiguationData":[TD([[makeQuery(id+"F13.imprint","IMPRINT",EDGE,{"derivedFrom":sQuery(id+"F13.wireOp",EDGE,"E48.0.8.0")}),-1.0]])]});
            var Q7;
            Q7=makeQuery(id+"F13.imprint","IMPRINT",FACE,{"disambiguationData":[TD([[makeQuery(id+"F13.imprint","IMPRINT",EDGE,{"derivedFrom":sQuery(id+"F13.wireOp",EDGE,"E48.0.9.0")}),-1.0]])]});
            var Q8;
            Q8=makeQuery(id+"F13.imprint","IMPRINT",FACE,{"disambiguationData":[TD([[makeQuery(id+"F13.imprint","IMPRINT",EDGE,{"derivedFrom":sQuery(id+"F13.wireOp",EDGE,"E48.0.6.0")}),-1.0]])]});
            var Q9;
            Q9=makeQuery(id+"F13.imprint","IMPRINT",FACE,{"disambiguationData":[TD([[makeQuery(id+"F13.imprint","IMPRINT",EDGE,{"derivedFrom":sQuery(id+"F13.wireOp",EDGE,"E48.0.4.0")}),-1.0]])]});
            extrude(context, id + "F19", {"entities" : qUnion([Q0, Q1, Q2, Q3, Q4, Q5, Q6, Q7, Q8, Q9]), "oppositeDirection" : true, "depth" : 4 * mm});
        }
        {
            var Q0;
            Q0=makeQuery(id+"F19.opExtrude","SWEPT_BODY",BODY,{"disambiguationData":[OSD([sQuery(id+"F13.wireOp",EDGE,"E48.0.9.0"),sQuery(id+"F13.wireOp",EDGE,"E48.0.9.1"),sQuery(id+"F13.wireOp",EDGE,"E48.0.9.2"),sQuery(id+"F13.wireOp",EDGE,"E49.0.9.0")])]});
            transform(context, id + "F20", {"entities" : qUnion([Q0]), "transformType" : TransformType.TRANSLATION_3D, "dx" : 0 * mm, "dy" : 0 * mm, "dz" : 0 * mm, "makeCopy" : true});
        }
    });
